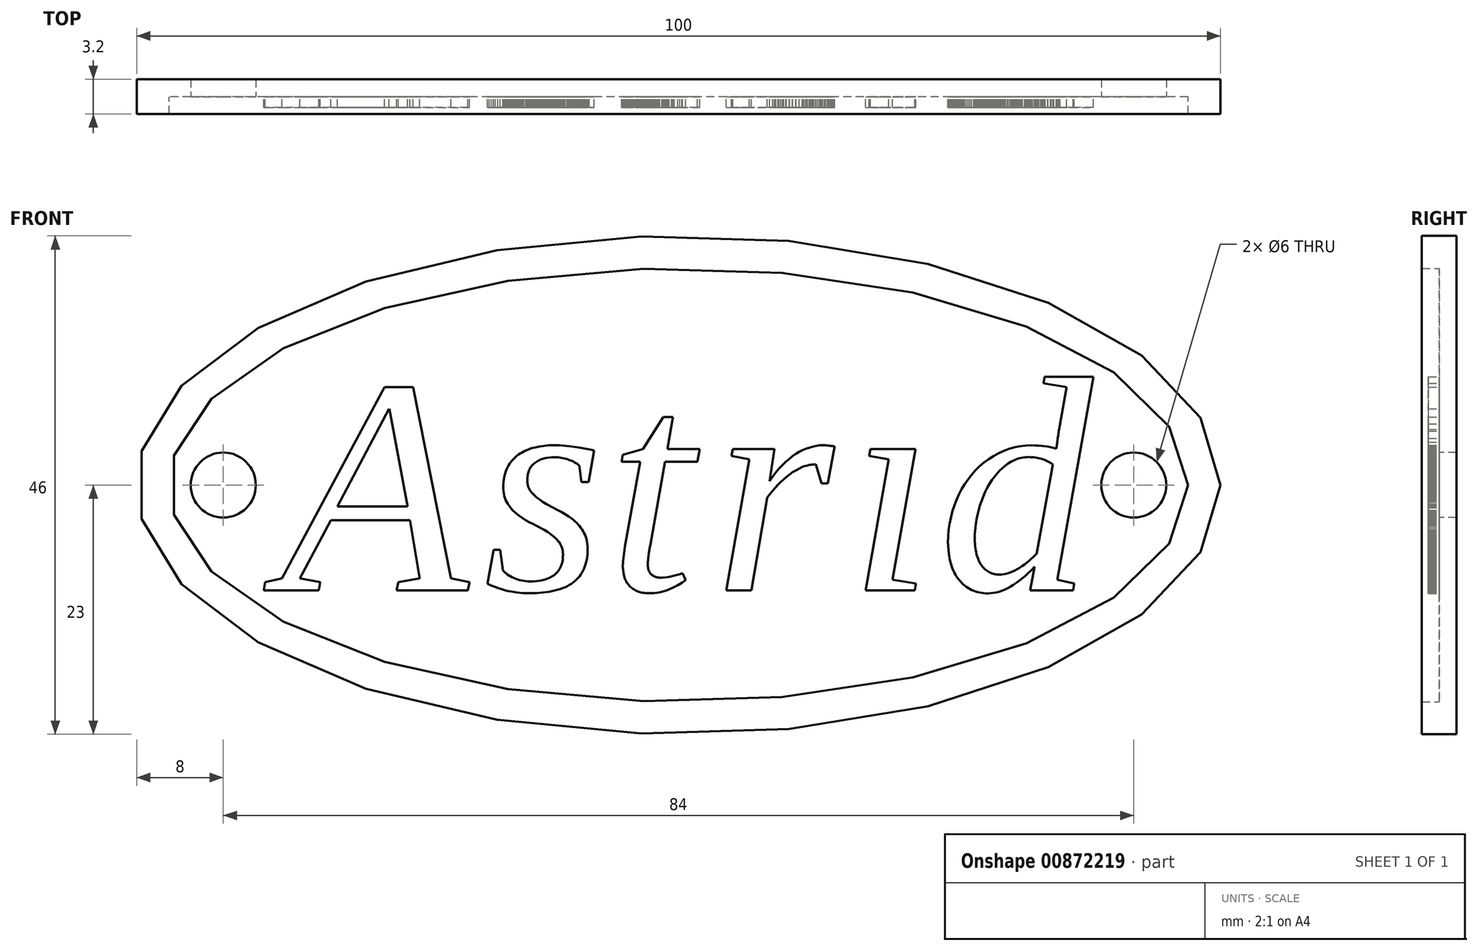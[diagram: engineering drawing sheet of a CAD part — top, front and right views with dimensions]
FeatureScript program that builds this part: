
annotation { "Feature Type Name" : "Feature", "Feature Type Description" : "" }
export const myFeature = defineFeature(function(context is Context, id is Id, definition is map)
    precondition{}
    {
        {
            var Q0;
            Q0=qCreatedBy(makeId("Front.planeOp"),FACE);
            var sketch = newSketch(context, id + "F0", { "sketchPlane" : qUnion([Q0])});
            skEllipse(sketch, "E0", {"center": v(0, 0) * mm, "majorRadius": 47 * mm, "minorRadius": 20 * mm, "majorAxis": v(1, 0)});
            skEllipse(sketch, "E1", {"center": v(0, 0) * mm, "majorRadius": 50 * mm, "minorRadius": 23 * mm, "majorAxis": v(1, 0)});
            skLineSegment(sketch, "E2", {"start": v(-81.12, 0) * mm, "end": v(85, 0) * mm, "construction": true});
            skPoint(sketch, "E2.startSnap0", {"position": v(-50, 0) * mm});
            skPoint(sketch, "E2.endSnap0", {"position": v(50, 0) * mm});
            skCircle(sketch, "E3", {"center": v(-42, 0) * mm, "radius": 3 * mm});
            skCircle(sketch, "E4", {"center": v(42, 0) * mm, "radius": 3 * mm});
            skLineSegment(sketch, "E5", {"start": v(-33.06, -8.97) * mm, "end": v(-33.2, -9.7) * mm});
            skLineSegment(sketch, "E6", {"start": v(-33.2, -9.7) * mm, "end": v(-38.27, -9.7) * mm});
            skLineSegment(sketch, "E7", {"start": v(-38.27, -9.7) * mm, "end": v(-38.14, -8.97) * mm});
            skLineSegment(sketch, "E8", {"start": v(-38.14, -8.97) * mm, "end": v(-36.58, -8.6) * mm});
            skLineSegment(sketch, "E9", {"start": v(-36.58, -8.6) * mm, "end": v(-27.12, 9.04) * mm});
            skLineSegment(sketch, "E10", {"start": v(-27.12, 9.04) * mm, "end": v(-24.47, 9.04) * mm});
            skLineSegment(sketch, "E11", {"start": v(-24.47, 9.04) * mm, "end": v(-21, -8.6) * mm});
            skLineSegment(sketch, "E12", {"start": v(-21, -8.6) * mm, "end": v(-19.27, -8.97) * mm});
            skLineSegment(sketch, "E13", {"start": v(-19.27, -8.97) * mm, "end": v(-19.43, -9.7) * mm});
            skLineSegment(sketch, "E14", {"start": v(-19.43, -9.7) * mm, "end": v(-26.01, -9.7) * mm});
            skLineSegment(sketch, "E15", {"start": v(-26.01, -9.7) * mm, "end": v(-25.86, -8.97) * mm});
            skLineSegment(sketch, "E16", {"start": v(-25.86, -8.97) * mm, "end": v(-23.88, -8.6) * mm});
            skLineSegment(sketch, "E17", {"start": v(-23.88, -8.6) * mm, "end": v(-24.77, -3.23) * mm});
            skLineSegment(sketch, "E18", {"start": v(-24.77, -3.23) * mm, "end": v(-32.09, -3.23) * mm});
            skLineSegment(sketch, "E19", {"start": v(-32.09, -3.23) * mm, "end": v(-34.93, -8.6) * mm});
            skLineSegment(sketch, "E20", {"start": v(-34.93, -8.6) * mm, "end": v(-33.06, -8.97) * mm});
            skLineSegment(sketch, "E21", {"start": v(-26.7, 7.05) * mm, "end": v(-31.46, -1.98) * mm});
            skLineSegment(sketch, "E22", {"start": v(-31.46, -1.98) * mm, "end": v(-24.99, -1.98) * mm});
            skLineSegment(sketch, "E23", {"start": v(-24.99, -1.98) * mm, "end": v(-26.7, 7.05) * mm});
            skLineSegment(sketch, "E24", {"start": v(-8.39, -5.88) * mm, "end": v(-8.4, -6.14) * mm});
            skLineSegment(sketch, "E25", {"start": v(-8.4, -6.14) * mm, "end": v(-8.4, -6.39) * mm});
            skLineSegment(sketch, "E26", {"start": v(-8.4, -6.39) * mm, "end": v(-8.43, -6.63) * mm});
            skLineSegment(sketch, "E27", {"start": v(-8.43, -6.63) * mm, "end": v(-8.47, -6.86) * mm});
            skLineSegment(sketch, "E28", {"start": v(-8.47, -6.86) * mm, "end": v(-8.52, -7.08) * mm});
            skLineSegment(sketch, "E29", {"start": v(-8.52, -7.08) * mm, "end": v(-8.57, -7.3) * mm});
            skLineSegment(sketch, "E30", {"start": v(-8.57, -7.3) * mm, "end": v(-8.64, -7.5) * mm});
            skLineSegment(sketch, "E31", {"start": v(-8.64, -7.5) * mm, "end": v(-8.72, -7.7) * mm});
            skLineSegment(sketch, "E32", {"start": v(-8.72, -7.7) * mm, "end": v(-8.8, -7.9) * mm});
            skLineSegment(sketch, "E33", {"start": v(-8.8, -7.9) * mm, "end": v(-8.9, -8.08) * mm});
            skLineSegment(sketch, "E34", {"start": v(-8.9, -8.08) * mm, "end": v(-9.01, -8.25) * mm});
            skLineSegment(sketch, "E35", {"start": v(-9.01, -8.25) * mm, "end": v(-9.13, -8.41) * mm});
            skLineSegment(sketch, "E36", {"start": v(-9.13, -8.41) * mm, "end": v(-9.26, -8.57) * mm});
            skLineSegment(sketch, "E37", {"start": v(-9.26, -8.57) * mm, "end": v(-9.4, -8.72) * mm});
            skLineSegment(sketch, "E38", {"start": v(-9.4, -8.72) * mm, "end": v(-9.56, -8.86) * mm});
            skLineSegment(sketch, "E39", {"start": v(-9.56, -8.86) * mm, "end": v(-9.72, -8.99) * mm});
            skLineSegment(sketch, "E40", {"start": v(-9.72, -8.99) * mm, "end": v(-9.89, -9.1) * mm});
            skLineSegment(sketch, "E41", {"start": v(-9.89, -9.1) * mm, "end": v(-10.07, -9.22) * mm});
            skLineSegment(sketch, "E42", {"start": v(-10.07, -9.22) * mm, "end": v(-10.26, -9.33) * mm});
            skLineSegment(sketch, "E43", {"start": v(-10.26, -9.33) * mm, "end": v(-10.47, -9.42) * mm});
            skLineSegment(sketch, "E44", {"start": v(-10.47, -9.42) * mm, "end": v(-10.68, -9.51) * mm});
            skLineSegment(sketch, "E45", {"start": v(-10.68, -9.51) * mm, "end": v(-10.9, -9.6) * mm});
            skLineSegment(sketch, "E46", {"start": v(-10.9, -9.6) * mm, "end": v(-11.14, -9.67) * mm});
            skLineSegment(sketch, "E47", {"start": v(-11.14, -9.67) * mm, "end": v(-11.4, -9.74) * mm});
            skLineSegment(sketch, "E48", {"start": v(-11.4, -9.74) * mm, "end": v(-11.65, -9.8) * mm});
            skLineSegment(sketch, "E49", {"start": v(-11.65, -9.8) * mm, "end": v(-11.92, -9.85) * mm});
            skLineSegment(sketch, "E50", {"start": v(-11.92, -9.85) * mm, "end": v(-12.2, -9.89) * mm});
            skLineSegment(sketch, "E51", {"start": v(-12.2, -9.89) * mm, "end": v(-12.49, -9.92) * mm});
            skLineSegment(sketch, "E52", {"start": v(-12.49, -9.92) * mm, "end": v(-13.1, -9.97) * mm});
            skLineSegment(sketch, "E53", {"start": v(-13.1, -9.97) * mm, "end": v(-13.75, -9.99) * mm});
            skLineSegment(sketch, "E54", {"start": v(-13.75, -9.99) * mm, "end": v(-14.36, -9.97) * mm});
            skLineSegment(sketch, "E55", {"start": v(-14.36, -9.97) * mm, "end": v(-14.94, -9.92) * mm});
            skLineSegment(sketch, "E56", {"start": v(-14.94, -9.92) * mm, "end": v(-15.48, -9.83) * mm});
            skLineSegment(sketch, "E57", {"start": v(-15.48, -9.83) * mm, "end": v(-15.74, -9.77) * mm});
            skLineSegment(sketch, "E58", {"start": v(-15.74, -9.77) * mm, "end": v(-15.99, -9.7) * mm});
            skLineSegment(sketch, "E59", {"start": v(-15.99, -9.7) * mm, "end": v(-16.46, -9.56) * mm});
            skLineSegment(sketch, "E60", {"start": v(-16.46, -9.56) * mm, "end": v(-16.68, -9.5) * mm});
            skLineSegment(sketch, "E61", {"start": v(-16.68, -9.5) * mm, "end": v(-16.9, -9.42) * mm});
            skLineSegment(sketch, "E62", {"start": v(-16.9, -9.42) * mm, "end": v(-17.1, -9.34) * mm});
            skLineSegment(sketch, "E63", {"start": v(-17.1, -9.34) * mm, "end": v(-17.28, -9.27) * mm});
            skLineSegment(sketch, "E64", {"start": v(-17.28, -9.27) * mm, "end": v(-17.46, -9.2) * mm});
            skLineSegment(sketch, "E65", {"start": v(-17.46, -9.2) * mm, "end": v(-17.64, -9.13) * mm});
            skLineSegment(sketch, "E66", {"start": v(-17.64, -9.13) * mm, "end": v(-17.07, -6) * mm});
            skLineSegment(sketch, "E67", {"start": v(-17.07, -6) * mm, "end": v(-16.44, -6) * mm});
            skLineSegment(sketch, "E68", {"start": v(-16.44, -6) * mm, "end": v(-16.2, -7.9) * mm});
            skLineSegment(sketch, "E69", {"start": v(-16.2, -7.9) * mm, "end": v(-16.11, -7.99) * mm});
            skLineSegment(sketch, "E70", {"start": v(-16.11, -7.99) * mm, "end": v(-16, -8.08) * mm});
            skLineSegment(sketch, "E71", {"start": v(-16, -8.08) * mm, "end": v(-15.9, -8.17) * mm});
            skLineSegment(sketch, "E72", {"start": v(-15.9, -8.17) * mm, "end": v(-15.77, -8.26) * mm});
            skLineSegment(sketch, "E73", {"start": v(-15.77, -8.26) * mm, "end": v(-15.64, -8.34) * mm});
            skLineSegment(sketch, "E74", {"start": v(-15.64, -8.34) * mm, "end": v(-15.5, -8.43) * mm});
            skLineSegment(sketch, "E75", {"start": v(-15.5, -8.43) * mm, "end": v(-15.35, -8.5) * mm});
            skLineSegment(sketch, "E76", {"start": v(-15.35, -8.5) * mm, "end": v(-15.2, -8.59) * mm});
            skLineSegment(sketch, "E77", {"start": v(-15.2, -8.59) * mm, "end": v(-15.03, -8.66) * mm});
            skLineSegment(sketch, "E78", {"start": v(-15.03, -8.66) * mm, "end": v(-14.85, -8.72) * mm});
            skLineSegment(sketch, "E79", {"start": v(-14.85, -8.72) * mm, "end": v(-14.67, -8.77) * mm});
            skLineSegment(sketch, "E80", {"start": v(-14.67, -8.77) * mm, "end": v(-14.49, -8.81) * mm});
            skLineSegment(sketch, "E81", {"start": v(-14.49, -8.81) * mm, "end": v(-14.3, -8.85) * mm});
            skLineSegment(sketch, "E82", {"start": v(-14.3, -8.85) * mm, "end": v(-14.1, -8.87) * mm});
            skLineSegment(sketch, "E83", {"start": v(-14.1, -8.87) * mm, "end": v(-13.9, -8.89) * mm});
            skLineSegment(sketch, "E84", {"start": v(-13.9, -8.89) * mm, "end": v(-13.7, -8.9) * mm});
            skLineSegment(sketch, "E85", {"start": v(-13.7, -8.9) * mm, "end": v(-13.39, -8.88) * mm});
            skLineSegment(sketch, "E86", {"start": v(-13.39, -8.88) * mm, "end": v(-13.1, -8.86) * mm});
            skLineSegment(sketch, "E87", {"start": v(-13.1, -8.86) * mm, "end": v(-12.8, -8.82) * mm});
            skLineSegment(sketch, "E88", {"start": v(-12.8, -8.82) * mm, "end": v(-12.52, -8.77) * mm});
            skLineSegment(sketch, "E89", {"start": v(-12.52, -8.77) * mm, "end": v(-12.38, -8.73) * mm});
            skLineSegment(sketch, "E90", {"start": v(-12.38, -8.73) * mm, "end": v(-12.25, -8.7) * mm});
            skLineSegment(sketch, "E91", {"start": v(-12.25, -8.7) * mm, "end": v(-12.12, -8.65) * mm});
            skLineSegment(sketch, "E92", {"start": v(-12.12, -8.65) * mm, "end": v(-12, -8.6) * mm});
            skLineSegment(sketch, "E93", {"start": v(-12, -8.6) * mm, "end": v(-11.88, -8.55) * mm});
            skLineSegment(sketch, "E94", {"start": v(-11.88, -8.55) * mm, "end": v(-11.76, -8.5) * mm});
            skLineSegment(sketch, "E95", {"start": v(-11.76, -8.5) * mm, "end": v(-11.65, -8.43) * mm});
            skLineSegment(sketch, "E96", {"start": v(-11.65, -8.43) * mm, "end": v(-11.55, -8.36) * mm});
            skLineSegment(sketch, "E97", {"start": v(-11.55, -8.36) * mm, "end": v(-11.45, -8.29) * mm});
            skLineSegment(sketch, "E98", {"start": v(-11.45, -8.29) * mm, "end": v(-11.35, -8.2) * mm});
            skLineSegment(sketch, "E99", {"start": v(-11.35, -8.2) * mm, "end": v(-11.26, -8.12) * mm});
            skLineSegment(sketch, "E100", {"start": v(-11.26, -8.12) * mm, "end": v(-11.18, -8.03) * mm});
            skLineSegment(sketch, "E101", {"start": v(-11.18, -8.03) * mm, "end": v(-11.1, -7.93) * mm});
            skLineSegment(sketch, "E102", {"start": v(-11.1, -7.93) * mm, "end": v(-11.02, -7.83) * mm});
            skLineSegment(sketch, "E103", {"start": v(-11.02, -7.83) * mm, "end": v(-10.96, -7.72) * mm});
            skLineSegment(sketch, "E104", {"start": v(-10.96, -7.72) * mm, "end": v(-10.9, -7.6) * mm});
            skLineSegment(sketch, "E105", {"start": v(-10.9, -7.6) * mm, "end": v(-10.84, -7.48) * mm});
            skLineSegment(sketch, "E106", {"start": v(-10.84, -7.48) * mm, "end": v(-10.8, -7.34) * mm});
            skLineSegment(sketch, "E107", {"start": v(-10.8, -7.34) * mm, "end": v(-10.75, -7.2) * mm});
            skLineSegment(sketch, "E108", {"start": v(-10.75, -7.2) * mm, "end": v(-10.72, -7.06) * mm});
            skLineSegment(sketch, "E109", {"start": v(-10.72, -7.06) * mm, "end": v(-10.7, -6.9) * mm});
            skLineSegment(sketch, "E110", {"start": v(-10.7, -6.9) * mm, "end": v(-10.67, -6.75) * mm});
            skLineSegment(sketch, "E111", {"start": v(-10.67, -6.75) * mm, "end": v(-10.66, -6.58) * mm});
            skLineSegment(sketch, "E112", {"start": v(-10.66, -6.58) * mm, "end": v(-10.66, -6.4) * mm});
            skLineSegment(sketch, "E113", {"start": v(-10.66, -6.4) * mm, "end": v(-10.67, -6.23) * mm});
            skLineSegment(sketch, "E114", {"start": v(-10.67, -6.23) * mm, "end": v(-10.67, -6.15) * mm});
            skLineSegment(sketch, "E115", {"start": v(-10.67, -6.15) * mm, "end": v(-10.69, -6.06) * mm});
            skLineSegment(sketch, "E116", {"start": v(-10.69, -6.06) * mm, "end": v(-10.7, -5.98) * mm});
            skLineSegment(sketch, "E117", {"start": v(-10.7, -5.98) * mm, "end": v(-10.72, -5.9) * mm});
            skLineSegment(sketch, "E118", {"start": v(-10.72, -5.9) * mm, "end": v(-10.74, -5.82) * mm});
            skLineSegment(sketch, "E119", {"start": v(-10.74, -5.82) * mm, "end": v(-10.76, -5.75) * mm});
            skLineSegment(sketch, "E120", {"start": v(-10.76, -5.75) * mm, "end": v(-10.8, -5.67) * mm});
            skLineSegment(sketch, "E121", {"start": v(-10.8, -5.67) * mm, "end": v(-10.82, -5.6) * mm});
            skLineSegment(sketch, "E122", {"start": v(-10.82, -5.6) * mm, "end": v(-10.86, -5.53) * mm});
            skLineSegment(sketch, "E123", {"start": v(-10.86, -5.53) * mm, "end": v(-10.9, -5.46) * mm});
            skLineSegment(sketch, "E124", {"start": v(-10.9, -5.46) * mm, "end": v(-10.93, -5.4) * mm});
            skLineSegment(sketch, "E125", {"start": v(-10.93, -5.4) * mm, "end": v(-10.98, -5.33) * mm});
            skLineSegment(sketch, "E126", {"start": v(-10.98, -5.33) * mm, "end": v(-11.03, -5.26) * mm});
            skLineSegment(sketch, "E127", {"start": v(-11.03, -5.26) * mm, "end": v(-11.08, -5.2) * mm});
            skLineSegment(sketch, "E128", {"start": v(-11.08, -5.2) * mm, "end": v(-11.18, -5.08) * mm});
            skLineSegment(sketch, "E129", {"start": v(-11.18, -5.08) * mm, "end": v(-11.3, -4.97) * mm});
            skLineSegment(sketch, "E130", {"start": v(-11.3, -4.97) * mm, "end": v(-11.4, -4.85) * mm});
            skLineSegment(sketch, "E131", {"start": v(-11.4, -4.85) * mm, "end": v(-11.53, -4.74) * mm});
            skLineSegment(sketch, "E132", {"start": v(-11.53, -4.74) * mm, "end": v(-11.66, -4.64) * mm});
            skLineSegment(sketch, "E133", {"start": v(-11.66, -4.64) * mm, "end": v(-11.94, -4.44) * mm});
            skLineSegment(sketch, "E134", {"start": v(-11.94, -4.44) * mm, "end": v(-12.09, -4.34) * mm});
            skLineSegment(sketch, "E135", {"start": v(-12.09, -4.34) * mm, "end": v(-12.4, -4.15) * mm});
            skLineSegment(sketch, "E136", {"start": v(-12.4, -4.15) * mm, "end": v(-13.07, -3.78) * mm});
            skLineSegment(sketch, "E137", {"start": v(-13.07, -3.78) * mm, "end": v(-13.42, -3.6) * mm});
            skLineSegment(sketch, "E138", {"start": v(-13.42, -3.6) * mm, "end": v(-13.77, -3.43) * mm});
            skLineSegment(sketch, "E139", {"start": v(-13.77, -3.43) * mm, "end": v(-14.1, -3.24) * mm});
            skLineSegment(sketch, "E140", {"start": v(-14.1, -3.24) * mm, "end": v(-14.43, -3.03) * mm});
            skLineSegment(sketch, "E141", {"start": v(-14.43, -3.03) * mm, "end": v(-14.74, -2.82) * mm});
            skLineSegment(sketch, "E142", {"start": v(-14.74, -2.82) * mm, "end": v(-15.03, -2.58) * mm});
            skLineSegment(sketch, "E143", {"start": v(-15.03, -2.58) * mm, "end": v(-15.3, -2.32) * mm});
            skLineSegment(sketch, "E144", {"start": v(-15.3, -2.32) * mm, "end": v(-15.54, -2.04) * mm});
            skLineSegment(sketch, "E145", {"start": v(-15.54, -2.04) * mm, "end": v(-15.76, -1.73) * mm});
            skLineSegment(sketch, "E146", {"start": v(-15.76, -1.73) * mm, "end": v(-15.86, -1.57) * mm});
            skLineSegment(sketch, "E147", {"start": v(-15.86, -1.57) * mm, "end": v(-15.94, -1.4) * mm});
            skLineSegment(sketch, "E148", {"start": v(-15.94, -1.4) * mm, "end": v(-16, -1.22) * mm});
            skLineSegment(sketch, "E149", {"start": v(-16, -1.22) * mm, "end": v(-16.07, -1.03) * mm});
            skLineSegment(sketch, "E150", {"start": v(-16.07, -1.03) * mm, "end": v(-16.1, -0.83) * mm});
            skLineSegment(sketch, "E151", {"start": v(-16.1, -0.83) * mm, "end": v(-16.14, -0.62) * mm});
            skLineSegment(sketch, "E152", {"start": v(-16.14, -0.62) * mm, "end": v(-16.16, -0.4) * mm});
            skLineSegment(sketch, "E153", {"start": v(-16.16, -0.4) * mm, "end": v(-16.17, -0.17) * mm});
            skLineSegment(sketch, "E154", {"start": v(-16.17, -0.17) * mm, "end": v(-16.16, 0.09) * mm});
            skLineSegment(sketch, "E155", {"start": v(-16.16, 0.09) * mm, "end": v(-16.14, 0.33) * mm});
            skLineSegment(sketch, "E156", {"start": v(-16.14, 0.33) * mm, "end": v(-16.11, 0.57) * mm});
            skLineSegment(sketch, "E157", {"start": v(-16.11, 0.57) * mm, "end": v(-16.07, 0.8) * mm});
            skLineSegment(sketch, "E158", {"start": v(-16.07, 0.8) * mm, "end": v(-16.02, 1.01) * mm});
            skLineSegment(sketch, "E159", {"start": v(-16.02, 1.01) * mm, "end": v(-15.96, 1.22) * mm});
            skLineSegment(sketch, "E160", {"start": v(-15.96, 1.22) * mm, "end": v(-15.88, 1.42) * mm});
            skLineSegment(sketch, "E161", {"start": v(-15.88, 1.42) * mm, "end": v(-15.8, 1.6) * mm});
            skLineSegment(sketch, "E162", {"start": v(-15.8, 1.6) * mm, "end": v(-15.7, 1.79) * mm});
            skLineSegment(sketch, "E163", {"start": v(-15.7, 1.79) * mm, "end": v(-15.58, 1.96) * mm});
            skLineSegment(sketch, "E164", {"start": v(-15.58, 1.96) * mm, "end": v(-15.47, 2.12) * mm});
            skLineSegment(sketch, "E165", {"start": v(-15.47, 2.12) * mm, "end": v(-15.34, 2.27) * mm});
            skLineSegment(sketch, "E166", {"start": v(-15.34, 2.27) * mm, "end": v(-15.2, 2.42) * mm});
            skLineSegment(sketch, "E167", {"start": v(-15.2, 2.42) * mm, "end": v(-15.07, 2.56) * mm});
            skLineSegment(sketch, "E168", {"start": v(-15.07, 2.56) * mm, "end": v(-14.92, 2.68) * mm});
            skLineSegment(sketch, "E169", {"start": v(-14.92, 2.68) * mm, "end": v(-14.77, 2.8) * mm});
            skLineSegment(sketch, "E170", {"start": v(-14.77, 2.8) * mm, "end": v(-14.6, 2.91) * mm});
            skLineSegment(sketch, "E171", {"start": v(-14.6, 2.91) * mm, "end": v(-14.43, 3.01) * mm});
            skLineSegment(sketch, "E172", {"start": v(-14.43, 3.01) * mm, "end": v(-14.25, 3.1) * mm});
            skLineSegment(sketch, "E173", {"start": v(-14.25, 3.1) * mm, "end": v(-14.07, 3.2) * mm});
            skLineSegment(sketch, "E174", {"start": v(-14.07, 3.2) * mm, "end": v(-13.88, 3.28) * mm});
            skLineSegment(sketch, "E175", {"start": v(-13.88, 3.28) * mm, "end": v(-13.69, 3.35) * mm});
            skLineSegment(sketch, "E176", {"start": v(-13.69, 3.35) * mm, "end": v(-13.49, 3.41) * mm});
            skLineSegment(sketch, "E177", {"start": v(-13.49, 3.41) * mm, "end": v(-13.28, 3.47) * mm});
            skLineSegment(sketch, "E178", {"start": v(-13.28, 3.47) * mm, "end": v(-12.85, 3.56) * mm});
            skLineSegment(sketch, "E179", {"start": v(-12.85, 3.56) * mm, "end": v(-12.41, 3.62) * mm});
            skLineSegment(sketch, "E180", {"start": v(-12.41, 3.62) * mm, "end": v(-11.97, 3.66) * mm});
            skLineSegment(sketch, "E181", {"start": v(-11.97, 3.66) * mm, "end": v(-11.5, 3.68) * mm});
            skLineSegment(sketch, "E182", {"start": v(-11.5, 3.68) * mm, "end": v(-11.01, 3.67) * mm});
            skLineSegment(sketch, "E183", {"start": v(-11.01, 3.67) * mm, "end": v(-10.05, 3.59) * mm});
            skLineSegment(sketch, "E184", {"start": v(-10.05, 3.59) * mm, "end": v(-9.58, 3.52) * mm});
            skLineSegment(sketch, "E185", {"start": v(-9.58, 3.52) * mm, "end": v(-9.12, 3.45) * mm});
            skLineSegment(sketch, "E186", {"start": v(-9.12, 3.45) * mm, "end": v(-8.22, 3.28) * mm});
            skLineSegment(sketch, "E187", {"start": v(-8.22, 3.28) * mm, "end": v(-7.79, 3.2) * mm});
            skLineSegment(sketch, "E188", {"start": v(-7.79, 3.2) * mm, "end": v(-8.3, 0.3) * mm});
            skLineSegment(sketch, "E189", {"start": v(-8.3, 0.3) * mm, "end": v(-8.95, 0.3) * mm});
            skLineSegment(sketch, "E190", {"start": v(-8.95, 0.3) * mm, "end": v(-9.15, 1.79) * mm});
            skLineSegment(sketch, "E191", {"start": v(-9.15, 1.79) * mm, "end": v(-9.25, 1.87) * mm});
            skLineSegment(sketch, "E192", {"start": v(-9.25, 1.87) * mm, "end": v(-9.36, 1.95) * mm});
            skLineSegment(sketch, "E193", {"start": v(-9.36, 1.95) * mm, "end": v(-9.47, 2.03) * mm});
            skLineSegment(sketch, "E194", {"start": v(-9.47, 2.03) * mm, "end": v(-9.6, 2.1) * mm});
            skLineSegment(sketch, "E195", {"start": v(-9.6, 2.1) * mm, "end": v(-9.72, 2.17) * mm});
            skLineSegment(sketch, "E196", {"start": v(-9.72, 2.17) * mm, "end": v(-9.86, 2.23) * mm});
            skLineSegment(sketch, "E197", {"start": v(-9.86, 2.23) * mm, "end": v(-10, 2.29) * mm});
            skLineSegment(sketch, "E198", {"start": v(-10, 2.29) * mm, "end": v(-10.15, 2.34) * mm});
            skLineSegment(sketch, "E199", {"start": v(-10.15, 2.34) * mm, "end": v(-10.3, 2.4) * mm});
            skLineSegment(sketch, "E200", {"start": v(-10.3, 2.4) * mm, "end": v(-10.45, 2.44) * mm});
            skLineSegment(sketch, "E201", {"start": v(-10.45, 2.44) * mm, "end": v(-10.6, 2.48) * mm});
            skLineSegment(sketch, "E202", {"start": v(-10.6, 2.48) * mm, "end": v(-10.77, 2.51) * mm});
            skLineSegment(sketch, "E203", {"start": v(-10.77, 2.51) * mm, "end": v(-10.94, 2.53) * mm});
            skLineSegment(sketch, "E204", {"start": v(-10.94, 2.53) * mm, "end": v(-11.1, 2.55) * mm});
            skLineSegment(sketch, "E205", {"start": v(-11.1, 2.55) * mm, "end": v(-11.28, 2.56) * mm});
            skLineSegment(sketch, "E206", {"start": v(-11.28, 2.56) * mm, "end": v(-11.45, 2.57) * mm});
            skLineSegment(sketch, "E207", {"start": v(-11.45, 2.57) * mm, "end": v(-11.73, 2.56) * mm});
            skLineSegment(sketch, "E208", {"start": v(-11.73, 2.56) * mm, "end": v(-12, 2.53) * mm});
            skLineSegment(sketch, "E209", {"start": v(-12, 2.53) * mm, "end": v(-12.24, 2.5) * mm});
            skLineSegment(sketch, "E210", {"start": v(-12.24, 2.5) * mm, "end": v(-12.36, 2.46) * mm});
            skLineSegment(sketch, "E211", {"start": v(-12.36, 2.46) * mm, "end": v(-12.47, 2.43) * mm});
            skLineSegment(sketch, "E212", {"start": v(-12.47, 2.43) * mm, "end": v(-12.59, 2.4) * mm});
            skLineSegment(sketch, "E213", {"start": v(-12.59, 2.4) * mm, "end": v(-12.7, 2.36) * mm});
            skLineSegment(sketch, "E214", {"start": v(-12.7, 2.36) * mm, "end": v(-12.8, 2.32) * mm});
            skLineSegment(sketch, "E215", {"start": v(-12.8, 2.32) * mm, "end": v(-12.9, 2.27) * mm});
            skLineSegment(sketch, "E216", {"start": v(-12.9, 2.27) * mm, "end": v(-13, 2.22) * mm});
            skLineSegment(sketch, "E217", {"start": v(-13, 2.22) * mm, "end": v(-13.1, 2.16) * mm});
            skLineSegment(sketch, "E218", {"start": v(-13.1, 2.16) * mm, "end": v(-13.18, 2.1) * mm});
            skLineSegment(sketch, "E219", {"start": v(-13.18, 2.1) * mm, "end": v(-13.27, 2.04) * mm});
            skLineSegment(sketch, "E220", {"start": v(-13.27, 2.04) * mm, "end": v(-13.35, 1.97) * mm});
            skLineSegment(sketch, "E221", {"start": v(-13.35, 1.97) * mm, "end": v(-13.43, 1.9) * mm});
            skLineSegment(sketch, "E222", {"start": v(-13.43, 1.9) * mm, "end": v(-13.5, 1.83) * mm});
            skLineSegment(sketch, "E223", {"start": v(-13.5, 1.83) * mm, "end": v(-13.56, 1.75) * mm});
            skLineSegment(sketch, "E224", {"start": v(-13.56, 1.75) * mm, "end": v(-13.63, 1.66) * mm});
            skLineSegment(sketch, "E225", {"start": v(-13.63, 1.66) * mm, "end": v(-13.68, 1.57) * mm});
            skLineSegment(sketch, "E226", {"start": v(-13.68, 1.57) * mm, "end": v(-13.73, 1.48) * mm});
            skLineSegment(sketch, "E227", {"start": v(-13.73, 1.48) * mm, "end": v(-13.78, 1.38) * mm});
            skLineSegment(sketch, "E228", {"start": v(-13.78, 1.38) * mm, "end": v(-13.82, 1.28) * mm});
            skLineSegment(sketch, "E229", {"start": v(-13.82, 1.28) * mm, "end": v(-13.85, 1.17) * mm});
            skLineSegment(sketch, "E230", {"start": v(-13.85, 1.17) * mm, "end": v(-13.88, 1.06) * mm});
            skLineSegment(sketch, "E231", {"start": v(-13.88, 1.06) * mm, "end": v(-13.9, 0.94) * mm});
            skLineSegment(sketch, "E232", {"start": v(-13.9, 0.94) * mm, "end": v(-13.92, 0.82) * mm});
            skLineSegment(sketch, "E233", {"start": v(-13.92, 0.82) * mm, "end": v(-13.94, 0.7) * mm});
            skLineSegment(sketch, "E234", {"start": v(-13.94, 0.7) * mm, "end": v(-13.94, 0.56) * mm});
            skLineSegment(sketch, "E235", {"start": v(-13.94, 0.56) * mm, "end": v(-13.95, 0.43) * mm});
            skLineSegment(sketch, "E236", {"start": v(-13.95, 0.43) * mm, "end": v(-13.94, 0.26) * mm});
            skLineSegment(sketch, "E237", {"start": v(-13.94, 0.26) * mm, "end": v(-13.93, 0.18) * mm});
            skLineSegment(sketch, "E238", {"start": v(-13.93, 0.18) * mm, "end": v(-13.92, 0.1) * mm});
            skLineSegment(sketch, "E239", {"start": v(-13.92, 0.1) * mm, "end": v(-13.9, 0.03) * mm});
            skLineSegment(sketch, "E240", {"start": v(-13.9, 0.03) * mm, "end": v(-13.9, -0.05) * mm});
            skLineSegment(sketch, "E241", {"start": v(-13.9, -0.05) * mm, "end": v(-13.87, -0.12) * mm});
            skLineSegment(sketch, "E242", {"start": v(-13.87, -0.12) * mm, "end": v(-13.85, -0.2) * mm});
            skLineSegment(sketch, "E243", {"start": v(-13.85, -0.2) * mm, "end": v(-13.82, -0.26) * mm});
            skLineSegment(sketch, "E244", {"start": v(-13.82, -0.26) * mm, "end": v(-13.79, -0.33) * mm});
            skLineSegment(sketch, "E245", {"start": v(-13.79, -0.33) * mm, "end": v(-13.76, -0.4) * mm});
            skLineSegment(sketch, "E246", {"start": v(-13.76, -0.4) * mm, "end": v(-13.72, -0.46) * mm});
            skLineSegment(sketch, "E247", {"start": v(-13.72, -0.46) * mm, "end": v(-13.68, -0.53) * mm});
            skLineSegment(sketch, "E248", {"start": v(-13.68, -0.53) * mm, "end": v(-13.64, -0.59) * mm});
            skLineSegment(sketch, "E249", {"start": v(-13.64, -0.59) * mm, "end": v(-13.6, -0.65) * mm});
            skLineSegment(sketch, "E250", {"start": v(-13.6, -0.65) * mm, "end": v(-13.54, -0.7) * mm});
            skLineSegment(sketch, "E251", {"start": v(-13.54, -0.7) * mm, "end": v(-13.32, -0.93) * mm});
            skLineSegment(sketch, "E252", {"start": v(-13.32, -0.93) * mm, "end": v(-13.08, -1.15) * mm});
            skLineSegment(sketch, "E253", {"start": v(-13.08, -1.15) * mm, "end": v(-12.8, -1.35) * mm});
            skLineSegment(sketch, "E254", {"start": v(-12.8, -1.35) * mm, "end": v(-12.5, -1.55) * mm});
            skLineSegment(sketch, "E255", {"start": v(-12.5, -1.55) * mm, "end": v(-12.19, -1.74) * mm});
            skLineSegment(sketch, "E256", {"start": v(-12.19, -1.74) * mm, "end": v(-11.52, -2.12) * mm});
            skLineSegment(sketch, "E257", {"start": v(-11.52, -2.12) * mm, "end": v(-11.17, -2.3) * mm});
            skLineSegment(sketch, "E258", {"start": v(-11.17, -2.3) * mm, "end": v(-10.82, -2.49) * mm});
            skLineSegment(sketch, "E259", {"start": v(-10.82, -2.49) * mm, "end": v(-10.48, -2.7) * mm});
            skLineSegment(sketch, "E260", {"start": v(-10.48, -2.7) * mm, "end": v(-10.15, -2.9) * mm});
            skLineSegment(sketch, "E261", {"start": v(-10.15, -2.9) * mm, "end": v(-9.83, -3.13) * mm});
            skLineSegment(sketch, "E262", {"start": v(-9.83, -3.13) * mm, "end": v(-9.68, -3.26) * mm});
            skLineSegment(sketch, "E263", {"start": v(-9.68, -3.26) * mm, "end": v(-9.53, -3.38) * mm});
            skLineSegment(sketch, "E264", {"start": v(-9.53, -3.38) * mm, "end": v(-9.4, -3.52) * mm});
            skLineSegment(sketch, "E265", {"start": v(-9.4, -3.52) * mm, "end": v(-9.26, -3.65) * mm});
            skLineSegment(sketch, "E266", {"start": v(-9.26, -3.65) * mm, "end": v(-9.13, -3.8) * mm});
            skLineSegment(sketch, "E267", {"start": v(-9.13, -3.8) * mm, "end": v(-9.02, -3.95) * mm});
            skLineSegment(sketch, "E268", {"start": v(-9.02, -3.95) * mm, "end": v(-8.9, -4.1) * mm});
            skLineSegment(sketch, "E269", {"start": v(-8.9, -4.1) * mm, "end": v(-8.8, -4.27) * mm});
            skLineSegment(sketch, "E270", {"start": v(-8.8, -4.27) * mm, "end": v(-8.7, -4.44) * mm});
            skLineSegment(sketch, "E271", {"start": v(-8.7, -4.44) * mm, "end": v(-8.62, -4.62) * mm});
            skLineSegment(sketch, "E272", {"start": v(-8.62, -4.62) * mm, "end": v(-8.55, -4.8) * mm});
            skLineSegment(sketch, "E273", {"start": v(-8.55, -4.8) * mm, "end": v(-8.49, -5) * mm});
            skLineSegment(sketch, "E274", {"start": v(-8.49, -5) * mm, "end": v(-8.44, -5.2) * mm});
            skLineSegment(sketch, "E275", {"start": v(-8.44, -5.2) * mm, "end": v(-8.41, -5.42) * mm});
            skLineSegment(sketch, "E276", {"start": v(-8.41, -5.42) * mm, "end": v(-8.4, -5.65) * mm});
            skLineSegment(sketch, "E277", {"start": v(-8.4, -5.65) * mm, "end": v(-8.39, -5.88) * mm});
            skLineSegment(sketch, "E278", {"start": v(-2.84, -7.3) * mm, "end": v(-2.84, -7.37) * mm});
            skLineSegment(sketch, "E279", {"start": v(-2.84, -7.37) * mm, "end": v(-2.83, -7.45) * mm});
            skLineSegment(sketch, "E280", {"start": v(-2.83, -7.45) * mm, "end": v(-2.83, -7.52) * mm});
            skLineSegment(sketch, "E281", {"start": v(-2.83, -7.52) * mm, "end": v(-2.82, -7.59) * mm});
            skLineSegment(sketch, "E282", {"start": v(-2.82, -7.59) * mm, "end": v(-2.8, -7.66) * mm});
            skLineSegment(sketch, "E283", {"start": v(-2.8, -7.66) * mm, "end": v(-2.8, -7.72) * mm});
            skLineSegment(sketch, "E284", {"start": v(-2.8, -7.72) * mm, "end": v(-2.78, -7.78) * mm});
            skLineSegment(sketch, "E285", {"start": v(-2.78, -7.78) * mm, "end": v(-2.76, -7.84) * mm});
            skLineSegment(sketch, "E286", {"start": v(-2.76, -7.84) * mm, "end": v(-2.74, -7.9) * mm});
            skLineSegment(sketch, "E287", {"start": v(-2.74, -7.9) * mm, "end": v(-2.72, -7.96) * mm});
            skLineSegment(sketch, "E288", {"start": v(-2.72, -7.96) * mm, "end": v(-2.7, -8) * mm});
            skLineSegment(sketch, "E289", {"start": v(-2.7, -8) * mm, "end": v(-2.67, -8.06) * mm});
            skLineSegment(sketch, "E290", {"start": v(-2.67, -8.06) * mm, "end": v(-2.64, -8.1) * mm});
            skLineSegment(sketch, "E291", {"start": v(-2.64, -8.1) * mm, "end": v(-2.6, -8.15) * mm});
            skLineSegment(sketch, "E292", {"start": v(-2.6, -8.15) * mm, "end": v(-2.57, -8.2) * mm});
            skLineSegment(sketch, "E293", {"start": v(-2.57, -8.2) * mm, "end": v(-2.53, -8.24) * mm});
            skLineSegment(sketch, "E294", {"start": v(-2.53, -8.24) * mm, "end": v(-2.5, -8.28) * mm});
            skLineSegment(sketch, "E295", {"start": v(-2.5, -8.28) * mm, "end": v(-2.45, -8.31) * mm});
            skLineSegment(sketch, "E296", {"start": v(-2.45, -8.31) * mm, "end": v(-2.4, -8.34) * mm});
            skLineSegment(sketch, "E297", {"start": v(-2.4, -8.34) * mm, "end": v(-2.36, -8.37) * mm});
            skLineSegment(sketch, "E298", {"start": v(-2.36, -8.37) * mm, "end": v(-2.32, -8.4) * mm});
            skLineSegment(sketch, "E299", {"start": v(-2.32, -8.4) * mm, "end": v(-2.27, -8.42) * mm});
            skLineSegment(sketch, "E300", {"start": v(-2.27, -8.42) * mm, "end": v(-2.22, -8.45) * mm});
            skLineSegment(sketch, "E301", {"start": v(-2.22, -8.45) * mm, "end": v(-2.17, -8.47) * mm});
            skLineSegment(sketch, "E302", {"start": v(-2.17, -8.47) * mm, "end": v(-2.12, -8.49) * mm});
            skLineSegment(sketch, "E303", {"start": v(-2.12, -8.49) * mm, "end": v(-2.07, -8.5) * mm});
            skLineSegment(sketch, "E304", {"start": v(-2.07, -8.5) * mm, "end": v(-2.01, -8.51) * mm});
            skLineSegment(sketch, "E305", {"start": v(-2.01, -8.51) * mm, "end": v(-1.96, -8.52) * mm});
            skLineSegment(sketch, "E306", {"start": v(-1.96, -8.52) * mm, "end": v(-1.9, -8.53) * mm});
            skLineSegment(sketch, "E307", {"start": v(-1.9, -8.53) * mm, "end": v(-1.85, -8.54) * mm});
            skLineSegment(sketch, "E308", {"start": v(-1.85, -8.54) * mm, "end": v(-1.79, -8.54) * mm});
            skLineSegment(sketch, "E309", {"start": v(-1.79, -8.54) * mm, "end": v(-1.73, -8.54) * mm});
            skLineSegment(sketch, "E310", {"start": v(-1.73, -8.54) * mm, "end": v(-1.43, -8.54) * mm});
            skLineSegment(sketch, "E311", {"start": v(-1.43, -8.54) * mm, "end": v(-1.15, -8.52) * mm});
            skLineSegment(sketch, "E312", {"start": v(-1.15, -8.52) * mm, "end": v(-0.89, -8.48) * mm});
            skLineSegment(sketch, "E313", {"start": v(-0.89, -8.48) * mm, "end": v(-0.63, -8.43) * mm});
            skLineSegment(sketch, "E314", {"start": v(-0.63, -8.43) * mm, "end": v(-0.38, -8.37) * mm});
            skLineSegment(sketch, "E315", {"start": v(-0.38, -8.37) * mm, "end": v(0.13, -8.22) * mm});
            skLineSegment(sketch, "E316", {"start": v(0.13, -8.22) * mm, "end": v(0.38, -8.13) * mm});
            skLineSegment(sketch, "E317", {"start": v(0.38, -8.13) * mm, "end": v(0.67, -8.78) * mm});
            skLineSegment(sketch, "E318", {"start": v(0.67, -8.78) * mm, "end": v(0.3, -9.02) * mm});
            skLineSegment(sketch, "E319", {"start": v(0.3, -9.02) * mm, "end": v(-0.07, -9.24) * mm});
            skLineSegment(sketch, "E320", {"start": v(-0.07, -9.24) * mm, "end": v(-0.47, -9.45) * mm});
            skLineSegment(sketch, "E321", {"start": v(-0.47, -9.45) * mm, "end": v(-0.88, -9.64) * mm});
            skLineSegment(sketch, "E322", {"start": v(-0.88, -9.64) * mm, "end": v(-1.1, -9.72) * mm});
            skLineSegment(sketch, "E323", {"start": v(-1.1, -9.72) * mm, "end": v(-1.31, -9.8) * mm});
            skLineSegment(sketch, "E324", {"start": v(-1.31, -9.8) * mm, "end": v(-1.54, -9.85) * mm});
            skLineSegment(sketch, "E325", {"start": v(-1.54, -9.85) * mm, "end": v(-1.77, -9.9) * mm});
            skLineSegment(sketch, "E326", {"start": v(-1.77, -9.9) * mm, "end": v(-2.01, -9.94) * mm});
            skLineSegment(sketch, "E327", {"start": v(-2.01, -9.94) * mm, "end": v(-2.26, -9.96) * mm});
            skLineSegment(sketch, "E328", {"start": v(-2.26, -9.96) * mm, "end": v(-2.52, -9.98) * mm});
            skLineSegment(sketch, "E329", {"start": v(-2.52, -9.98) * mm, "end": v(-2.78, -9.99) * mm});
            skLineSegment(sketch, "E330", {"start": v(-2.78, -9.99) * mm, "end": v(-2.92, -9.98) * mm});
            skLineSegment(sketch, "E331", {"start": v(-2.92, -9.98) * mm, "end": v(-3.06, -9.97) * mm});
            skLineSegment(sketch, "E332", {"start": v(-3.06, -9.97) * mm, "end": v(-3.2, -9.96) * mm});
            skLineSegment(sketch, "E333", {"start": v(-3.2, -9.96) * mm, "end": v(-3.33, -9.94) * mm});
            skLineSegment(sketch, "E334", {"start": v(-3.33, -9.94) * mm, "end": v(-3.46, -9.91) * mm});
            skLineSegment(sketch, "E335", {"start": v(-3.46, -9.91) * mm, "end": v(-3.58, -9.88) * mm});
            skLineSegment(sketch, "E336", {"start": v(-3.58, -9.88) * mm, "end": v(-3.7, -9.84) * mm});
            skLineSegment(sketch, "E337", {"start": v(-3.7, -9.84) * mm, "end": v(-3.8, -9.8) * mm});
            skLineSegment(sketch, "E338", {"start": v(-3.8, -9.8) * mm, "end": v(-3.92, -9.74) * mm});
            skLineSegment(sketch, "E339", {"start": v(-3.92, -9.74) * mm, "end": v(-4.02, -9.7) * mm});
            skLineSegment(sketch, "E340", {"start": v(-4.02, -9.7) * mm, "end": v(-4.12, -9.64) * mm});
            skLineSegment(sketch, "E341", {"start": v(-4.12, -9.64) * mm, "end": v(-4.22, -9.57) * mm});
            skLineSegment(sketch, "E342", {"start": v(-4.22, -9.57) * mm, "end": v(-4.3, -9.5) * mm});
            skLineSegment(sketch, "E343", {"start": v(-4.3, -9.5) * mm, "end": v(-4.4, -9.44) * mm});
            skLineSegment(sketch, "E344", {"start": v(-4.4, -9.44) * mm, "end": v(-4.48, -9.36) * mm});
            skLineSegment(sketch, "E345", {"start": v(-4.48, -9.36) * mm, "end": v(-4.56, -9.28) * mm});
            skLineSegment(sketch, "E346", {"start": v(-4.56, -9.28) * mm, "end": v(-4.63, -9.2) * mm});
            skLineSegment(sketch, "E347", {"start": v(-4.63, -9.2) * mm, "end": v(-4.7, -9.1) * mm});
            skLineSegment(sketch, "E348", {"start": v(-4.7, -9.1) * mm, "end": v(-4.76, -9.01) * mm});
            skLineSegment(sketch, "E349", {"start": v(-4.76, -9.01) * mm, "end": v(-4.81, -8.91) * mm});
            skLineSegment(sketch, "E350", {"start": v(-4.81, -8.91) * mm, "end": v(-4.87, -8.81) * mm});
            skLineSegment(sketch, "E351", {"start": v(-4.87, -8.81) * mm, "end": v(-4.92, -8.7) * mm});
            skLineSegment(sketch, "E352", {"start": v(-4.92, -8.7) * mm, "end": v(-4.96, -8.6) * mm});
            skLineSegment(sketch, "E353", {"start": v(-4.96, -8.6) * mm, "end": v(-5, -8.49) * mm});
            skLineSegment(sketch, "E354", {"start": v(-5, -8.49) * mm, "end": v(-5.06, -8.25) * mm});
            skLineSegment(sketch, "E355", {"start": v(-5.06, -8.25) * mm, "end": v(-5.1, -8) * mm});
            skLineSegment(sketch, "E356", {"start": v(-5.1, -8) * mm, "end": v(-5.13, -7.73) * mm});
            skLineSegment(sketch, "E357", {"start": v(-5.13, -7.73) * mm, "end": v(-5.14, -7.46) * mm});
            skLineSegment(sketch, "E358", {"start": v(-5.14, -7.46) * mm, "end": v(-5.13, -7.25) * mm});
            skLineSegment(sketch, "E359", {"start": v(-5.13, -7.25) * mm, "end": v(-5.12, -7.03) * mm});
            skLineSegment(sketch, "E360", {"start": v(-5.12, -7.03) * mm, "end": v(-5.1, -6.8) * mm});
            skLineSegment(sketch, "E361", {"start": v(-5.1, -6.8) * mm, "end": v(-5.07, -6.55) * mm});
            skLineSegment(sketch, "E362", {"start": v(-5.07, -6.55) * mm, "end": v(-5.03, -6.3) * mm});
            skLineSegment(sketch, "E363", {"start": v(-5.03, -6.3) * mm, "end": v(-4.96, -5.8) * mm});
            skLineSegment(sketch, "E364", {"start": v(-4.96, -5.8) * mm, "end": v(-4.92, -5.56) * mm});
            skLineSegment(sketch, "E365", {"start": v(-4.92, -5.56) * mm, "end": v(-3.54, 2.16) * mm});
            skLineSegment(sketch, "E366", {"start": v(-3.54, 2.16) * mm, "end": v(-5.25, 2.16) * mm});
            skLineSegment(sketch, "E367", {"start": v(-5.25, 2.16) * mm, "end": v(-5.14, 2.79) * mm});
            skLineSegment(sketch, "E368", {"start": v(-5.14, 2.79) * mm, "end": v(-3.3, 3.33) * mm});
            skLineSegment(sketch, "E369", {"start": v(-3.3, 3.33) * mm, "end": v(-1.4, 6.28) * mm});
            skLineSegment(sketch, "E370", {"start": v(-1.4, 6.28) * mm, "end": v(-0.5, 6.28) * mm});
            skLineSegment(sketch, "E371", {"start": v(-0.5, 6.28) * mm, "end": v(-1.02, 3.33) * mm});
            skLineSegment(sketch, "E372", {"start": v(-1.02, 3.33) * mm, "end": v(1.96, 3.33) * mm});
            skLineSegment(sketch, "E373", {"start": v(1.96, 3.33) * mm, "end": v(1.74, 2.16) * mm});
            skLineSegment(sketch, "E374", {"start": v(1.74, 2.16) * mm, "end": v(-1.24, 2.16) * mm});
            skLineSegment(sketch, "E375", {"start": v(-1.24, 2.16) * mm, "end": v(-2.59, -5.45) * mm});
            skLineSegment(sketch, "E376", {"start": v(-2.59, -5.45) * mm, "end": v(-2.64, -5.73) * mm});
            skLineSegment(sketch, "E377", {"start": v(-2.64, -5.73) * mm, "end": v(-2.73, -6.26) * mm});
            skLineSegment(sketch, "E378", {"start": v(-2.73, -6.26) * mm, "end": v(-2.77, -6.5) * mm});
            skLineSegment(sketch, "E379", {"start": v(-2.77, -6.5) * mm, "end": v(-2.78, -6.62) * mm});
            skLineSegment(sketch, "E380", {"start": v(-2.78, -6.62) * mm, "end": v(-2.8, -6.74) * mm});
            skLineSegment(sketch, "E381", {"start": v(-2.8, -6.74) * mm, "end": v(-2.8, -6.84) * mm});
            skLineSegment(sketch, "E382", {"start": v(-2.8, -6.84) * mm, "end": v(-2.82, -6.95) * mm});
            skLineSegment(sketch, "E383", {"start": v(-2.82, -6.95) * mm, "end": v(-2.83, -7.04) * mm});
            skLineSegment(sketch, "E384", {"start": v(-2.83, -7.04) * mm, "end": v(-2.83, -7.13) * mm});
            skLineSegment(sketch, "E385", {"start": v(-2.83, -7.13) * mm, "end": v(-2.84, -7.22) * mm});
            skLineSegment(sketch, "E386", {"start": v(-2.84, -7.22) * mm, "end": v(-2.84, -7.3) * mm});
            skLineSegment(sketch, "E387", {"start": v(13.3, 3.68) * mm, "end": v(13.44, 3.67) * mm});
            skLineSegment(sketch, "E388", {"start": v(13.44, 3.67) * mm, "end": v(13.59, 3.67) * mm});
            skLineSegment(sketch, "E389", {"start": v(13.59, 3.67) * mm, "end": v(13.74, 3.65) * mm});
            skLineSegment(sketch, "E390", {"start": v(13.74, 3.65) * mm, "end": v(13.9, 3.63) * mm});
            skLineSegment(sketch, "E391", {"start": v(13.9, 3.63) * mm, "end": v(13.99, 3.63) * mm});
            skLineSegment(sketch, "E392", {"start": v(13.99, 3.63) * mm, "end": v(14.06, 3.62) * mm});
            skLineSegment(sketch, "E393", {"start": v(14.06, 3.62) * mm, "end": v(14.13, 3.61) * mm});
            skLineSegment(sketch, "E394", {"start": v(14.13, 3.61) * mm, "end": v(14.16, 3.6) * mm});
            skLineSegment(sketch, "E395", {"start": v(14.16, 3.6) * mm, "end": v(14.2, 3.6) * mm});
            skLineSegment(sketch, "E396", {"start": v(14.2, 3.6) * mm, "end": v(14.22, 3.6) * mm});
            skLineSegment(sketch, "E397", {"start": v(14.22, 3.6) * mm, "end": v(14.25, 3.6) * mm});
            skLineSegment(sketch, "E398", {"start": v(14.25, 3.6) * mm, "end": v(14.28, 3.59) * mm});
            skLineSegment(sketch, "E399", {"start": v(14.28, 3.59) * mm, "end": v(14.3, 3.58) * mm});
            skLineSegment(sketch, "E400", {"start": v(14.3, 3.58) * mm, "end": v(14.33, 3.58) * mm});
            skLineSegment(sketch, "E401", {"start": v(14.33, 3.58) * mm, "end": v(14.35, 3.57) * mm});
            skLineSegment(sketch, "E402", {"start": v(14.35, 3.57) * mm, "end": v(14.37, 3.57) * mm});
            skLineSegment(sketch, "E403", {"start": v(14.37, 3.57) * mm, "end": v(14.4, 3.56) * mm});
            skLineSegment(sketch, "E404", {"start": v(14.4, 3.56) * mm, "end": v(13.78, 0.15) * mm});
            skLineSegment(sketch, "E405", {"start": v(13.78, 0.15) * mm, "end": v(13.18, 0.15) * mm});
            skLineSegment(sketch, "E406", {"start": v(13.18, 0.15) * mm, "end": v(12.66, 1.91) * mm});
            skLineSegment(sketch, "E407", {"start": v(12.66, 1.91) * mm, "end": v(12.5, 1.91) * mm});
            skLineSegment(sketch, "E408", {"start": v(12.5, 1.91) * mm, "end": v(12.35, 1.9) * mm});
            skLineSegment(sketch, "E409", {"start": v(12.35, 1.9) * mm, "end": v(12.2, 1.88) * mm});
            skLineSegment(sketch, "E410", {"start": v(12.2, 1.88) * mm, "end": v(12.05, 1.85) * mm});
            skLineSegment(sketch, "E411", {"start": v(12.05, 1.85) * mm, "end": v(11.9, 1.82) * mm});
            skLineSegment(sketch, "E412", {"start": v(11.9, 1.82) * mm, "end": v(11.74, 1.77) * mm});
            skLineSegment(sketch, "E413", {"start": v(11.74, 1.77) * mm, "end": v(11.59, 1.72) * mm});
            skLineSegment(sketch, "E414", {"start": v(11.59, 1.72) * mm, "end": v(11.44, 1.66) * mm});
            skLineSegment(sketch, "E415", {"start": v(11.44, 1.66) * mm, "end": v(11.13, 1.53) * mm});
            skLineSegment(sketch, "E416", {"start": v(11.13, 1.53) * mm, "end": v(10.84, 1.37) * mm});
            skLineSegment(sketch, "E417", {"start": v(10.84, 1.37) * mm, "end": v(10.54, 1.19) * mm});
            skLineSegment(sketch, "E418", {"start": v(10.54, 1.19) * mm, "end": v(10.26, 0.98) * mm});
            skLineSegment(sketch, "E419", {"start": v(10.26, 0.98) * mm, "end": v(9.98, 0.77) * mm});
            skLineSegment(sketch, "E420", {"start": v(9.98, 0.77) * mm, "end": v(9.7, 0.53) * mm});
            skLineSegment(sketch, "E421", {"start": v(9.7, 0.53) * mm, "end": v(9.43, 0.28) * mm});
            skLineSegment(sketch, "E422", {"start": v(9.43, 0.28) * mm, "end": v(9.16, 0.01) * mm});
            skLineSegment(sketch, "E423", {"start": v(9.16, 0.01) * mm, "end": v(8.9, -0.27) * mm});
            skLineSegment(sketch, "E424", {"start": v(8.9, -0.27) * mm, "end": v(8.42, -0.86) * mm});
            skLineSegment(sketch, "E425", {"start": v(8.42, -0.86) * mm, "end": v(8.2, -1.17) * mm});
            skLineSegment(sketch, "E426", {"start": v(8.2, -1.17) * mm, "end": v(6.7, -9.7) * mm});
            skLineSegment(sketch, "E427", {"start": v(6.7, -9.7) * mm, "end": v(4.4, -9.7) * mm});
            skLineSegment(sketch, "E428", {"start": v(4.4, -9.7) * mm, "end": v(6.53, 2.36) * mm});
            skLineSegment(sketch, "E429", {"start": v(6.53, 2.36) * mm, "end": v(4.89, 2.7) * mm});
            skLineSegment(sketch, "E430", {"start": v(4.89, 2.7) * mm, "end": v(5, 3.33) * mm});
            skLineSegment(sketch, "E431", {"start": v(5, 3.33) * mm, "end": v(8.84, 3.33) * mm});
            skLineSegment(sketch, "E432", {"start": v(8.84, 3.33) * mm, "end": v(8.41, 0.39) * mm});
            skLineSegment(sketch, "E433", {"start": v(8.41, 0.39) * mm, "end": v(8.7, 0.8) * mm});
            skLineSegment(sketch, "E434", {"start": v(8.7, 0.8) * mm, "end": v(8.98, 1.17) * mm});
            skLineSegment(sketch, "E435", {"start": v(8.98, 1.17) * mm, "end": v(9.28, 1.52) * mm});
            skLineSegment(sketch, "E436", {"start": v(9.28, 1.52) * mm, "end": v(9.58, 1.84) * mm});
            skLineSegment(sketch, "E437", {"start": v(9.58, 1.84) * mm, "end": v(9.89, 2.14) * mm});
            skLineSegment(sketch, "E438", {"start": v(9.89, 2.14) * mm, "end": v(10.2, 2.41) * mm});
            skLineSegment(sketch, "E439", {"start": v(10.2, 2.41) * mm, "end": v(10.51, 2.66) * mm});
            skLineSegment(sketch, "E440", {"start": v(10.51, 2.66) * mm, "end": v(10.83, 2.87) * mm});
            skLineSegment(sketch, "E441", {"start": v(10.83, 2.87) * mm, "end": v(11.14, 3.06) * mm});
            skLineSegment(sketch, "E442", {"start": v(11.14, 3.06) * mm, "end": v(11.45, 3.22) * mm});
            skLineSegment(sketch, "E443", {"start": v(11.45, 3.22) * mm, "end": v(11.76, 3.36) * mm});
            skLineSegment(sketch, "E444", {"start": v(11.76, 3.36) * mm, "end": v(12.07, 3.47) * mm});
            skLineSegment(sketch, "E445", {"start": v(12.07, 3.47) * mm, "end": v(12.39, 3.56) * mm});
            skLineSegment(sketch, "E446", {"start": v(12.39, 3.56) * mm, "end": v(12.7, 3.62) * mm});
            skLineSegment(sketch, "E447", {"start": v(12.7, 3.62) * mm, "end": v(12.85, 3.65) * mm});
            skLineSegment(sketch, "E448", {"start": v(12.85, 3.65) * mm, "end": v(13, 3.66) * mm});
            skLineSegment(sketch, "E449", {"start": v(13, 3.66) * mm, "end": v(13.15, 3.67) * mm});
            skLineSegment(sketch, "E450", {"start": v(13.15, 3.67) * mm, "end": v(13.3, 3.68) * mm});
            skLineSegment(sketch, "E451", {"start": v(19.73, -8.74) * mm, "end": v(21.9, -9.08) * mm});
            skLineSegment(sketch, "E452", {"start": v(21.9, -9.08) * mm, "end": v(21.8, -9.7) * mm});
            skLineSegment(sketch, "E453", {"start": v(21.8, -9.7) * mm, "end": v(17.26, -9.7) * mm});
            skLineSegment(sketch, "E454", {"start": v(17.26, -9.7) * mm, "end": v(19.38, 2.36) * mm});
            skLineSegment(sketch, "E455", {"start": v(19.38, 2.36) * mm, "end": v(17.6, 2.7) * mm});
            skLineSegment(sketch, "E456", {"start": v(17.6, 2.7) * mm, "end": v(17.7, 3.33) * mm});
            skLineSegment(sketch, "E457", {"start": v(17.7, 3.33) * mm, "end": v(21.85, 3.33) * mm});
            skLineSegment(sketch, "E458", {"start": v(21.85, 3.33) * mm, "end": v(19.73, -8.74) * mm});
            skLineSegment(sketch, "E459", {"start": v(22.71, 7.59) * mm, "end": v(22.71, 7.51) * mm});
            skLineSegment(sketch, "E460", {"start": v(22.71, 7.51) * mm, "end": v(22.7, 7.44) * mm});
            skLineSegment(sketch, "E461", {"start": v(22.7, 7.44) * mm, "end": v(22.7, 7.36) * mm});
            skLineSegment(sketch, "E462", {"start": v(22.7, 7.36) * mm, "end": v(22.68, 7.29) * mm});
            skLineSegment(sketch, "E463", {"start": v(22.68, 7.29) * mm, "end": v(22.66, 7.22) * mm});
            skLineSegment(sketch, "E464", {"start": v(22.66, 7.22) * mm, "end": v(22.64, 7.14) * mm});
            skLineSegment(sketch, "E465", {"start": v(22.64, 7.14) * mm, "end": v(22.62, 7.07) * mm});
            skLineSegment(sketch, "E466", {"start": v(22.62, 7.07) * mm, "end": v(22.59, 7) * mm});
            skLineSegment(sketch, "E467", {"start": v(22.59, 7) * mm, "end": v(22.56, 6.94) * mm});
            skLineSegment(sketch, "E468", {"start": v(22.56, 6.94) * mm, "end": v(22.53, 6.88) * mm});
            skLineSegment(sketch, "E469", {"start": v(22.53, 6.88) * mm, "end": v(22.5, 6.81) * mm});
            skLineSegment(sketch, "E470", {"start": v(22.5, 6.81) * mm, "end": v(22.45, 6.75) * mm});
            skLineSegment(sketch, "E471", {"start": v(22.45, 6.75) * mm, "end": v(22.41, 6.7) * mm});
            skLineSegment(sketch, "E472", {"start": v(22.41, 6.7) * mm, "end": v(22.37, 6.64) * mm});
            skLineSegment(sketch, "E473", {"start": v(22.37, 6.64) * mm, "end": v(22.32, 6.59) * mm});
            skLineSegment(sketch, "E474", {"start": v(22.32, 6.59) * mm, "end": v(22.27, 6.53) * mm});
            skLineSegment(sketch, "E475", {"start": v(22.27, 6.53) * mm, "end": v(22.22, 6.48) * mm});
            skLineSegment(sketch, "E476", {"start": v(22.22, 6.48) * mm, "end": v(22.16, 6.43) * mm});
            skLineSegment(sketch, "E477", {"start": v(22.16, 6.43) * mm, "end": v(22.1, 6.39) * mm});
            skLineSegment(sketch, "E478", {"start": v(22.1, 6.39) * mm, "end": v(22.04, 6.35) * mm});
            skLineSegment(sketch, "E479", {"start": v(22.04, 6.35) * mm, "end": v(21.98, 6.3) * mm});
            skLineSegment(sketch, "E480", {"start": v(21.98, 6.3) * mm, "end": v(21.92, 6.27) * mm});
            skLineSegment(sketch, "E481", {"start": v(21.92, 6.27) * mm, "end": v(21.85, 6.23) * mm});
            skLineSegment(sketch, "E482", {"start": v(21.85, 6.23) * mm, "end": v(21.78, 6.2) * mm});
            skLineSegment(sketch, "E483", {"start": v(21.78, 6.2) * mm, "end": v(21.71, 6.17) * mm});
            skLineSegment(sketch, "E484", {"start": v(21.71, 6.17) * mm, "end": v(21.64, 6.15) * mm});
            skLineSegment(sketch, "E485", {"start": v(21.64, 6.15) * mm, "end": v(21.57, 6.13) * mm});
            skLineSegment(sketch, "E486", {"start": v(21.57, 6.13) * mm, "end": v(21.5, 6.12) * mm});
            skLineSegment(sketch, "E487", {"start": v(21.5, 6.12) * mm, "end": v(21.43, 6.1) * mm});
            skLineSegment(sketch, "E488", {"start": v(21.43, 6.1) * mm, "end": v(21.35, 6.1) * mm});
            skLineSegment(sketch, "E489", {"start": v(21.35, 6.1) * mm, "end": v(21.28, 6.1) * mm});
            skLineSegment(sketch, "E490", {"start": v(21.28, 6.1) * mm, "end": v(21.2, 6.09) * mm});
            skLineSegment(sketch, "E491", {"start": v(21.2, 6.09) * mm, "end": v(21.12, 6.1) * mm});
            skLineSegment(sketch, "E492", {"start": v(21.12, 6.1) * mm, "end": v(21.05, 6.1) * mm});
            skLineSegment(sketch, "E493", {"start": v(21.05, 6.1) * mm, "end": v(20.98, 6.1) * mm});
            skLineSegment(sketch, "E494", {"start": v(20.98, 6.1) * mm, "end": v(20.9, 6.12) * mm});
            skLineSegment(sketch, "E495", {"start": v(20.9, 6.12) * mm, "end": v(20.83, 6.13) * mm});
            skLineSegment(sketch, "E496", {"start": v(20.83, 6.13) * mm, "end": v(20.76, 6.15) * mm});
            skLineSegment(sketch, "E497", {"start": v(20.76, 6.15) * mm, "end": v(20.69, 6.17) * mm});
            skLineSegment(sketch, "E498", {"start": v(20.69, 6.17) * mm, "end": v(20.62, 6.2) * mm});
            skLineSegment(sketch, "E499", {"start": v(20.62, 6.2) * mm, "end": v(20.49, 6.27) * mm});
            skLineSegment(sketch, "E500", {"start": v(20.49, 6.27) * mm, "end": v(20.37, 6.35) * mm});
            skLineSegment(sketch, "E501", {"start": v(20.37, 6.35) * mm, "end": v(20.25, 6.43) * mm});
            skLineSegment(sketch, "E502", {"start": v(20.25, 6.43) * mm, "end": v(20.15, 6.53) * mm});
            skLineSegment(sketch, "E503", {"start": v(20.15, 6.53) * mm, "end": v(20.05, 6.64) * mm});
            skLineSegment(sketch, "E504", {"start": v(20.05, 6.64) * mm, "end": v(19.96, 6.75) * mm});
            skLineSegment(sketch, "E505", {"start": v(19.96, 6.75) * mm, "end": v(19.88, 6.88) * mm});
            skLineSegment(sketch, "E506", {"start": v(19.88, 6.88) * mm, "end": v(19.81, 7) * mm});
            skLineSegment(sketch, "E507", {"start": v(19.81, 7) * mm, "end": v(19.79, 7.07) * mm});
            skLineSegment(sketch, "E508", {"start": v(19.79, 7.07) * mm, "end": v(19.77, 7.14) * mm});
            skLineSegment(sketch, "E509", {"start": v(19.77, 7.14) * mm, "end": v(19.75, 7.22) * mm});
            skLineSegment(sketch, "E510", {"start": v(19.75, 7.22) * mm, "end": v(19.73, 7.29) * mm});
            skLineSegment(sketch, "E511", {"start": v(19.73, 7.29) * mm, "end": v(19.72, 7.36) * mm});
            skLineSegment(sketch, "E512", {"start": v(19.72, 7.36) * mm, "end": v(19.7, 7.44) * mm});
            skLineSegment(sketch, "E513", {"start": v(19.7, 7.44) * mm, "end": v(19.7, 7.51) * mm});
            skLineSegment(sketch, "E514", {"start": v(19.7, 7.51) * mm, "end": v(19.7, 7.59) * mm});
            skLineSegment(sketch, "E515", {"start": v(19.7, 7.59) * mm, "end": v(19.7, 7.66) * mm});
            skLineSegment(sketch, "E516", {"start": v(19.7, 7.66) * mm, "end": v(19.7, 7.74) * mm});
            skLineSegment(sketch, "E517", {"start": v(19.7, 7.74) * mm, "end": v(19.72, 7.81) * mm});
            skLineSegment(sketch, "E518", {"start": v(19.72, 7.81) * mm, "end": v(19.73, 7.88) * mm});
            skLineSegment(sketch, "E519", {"start": v(19.73, 7.88) * mm, "end": v(19.75, 7.96) * mm});
            skLineSegment(sketch, "E520", {"start": v(19.75, 7.96) * mm, "end": v(19.77, 8.03) * mm});
            skLineSegment(sketch, "E521", {"start": v(19.77, 8.03) * mm, "end": v(19.79, 8.1) * mm});
            skLineSegment(sketch, "E522", {"start": v(19.79, 8.1) * mm, "end": v(19.81, 8.17) * mm});
            skLineSegment(sketch, "E523", {"start": v(19.81, 8.17) * mm, "end": v(19.85, 8.24) * mm});
            skLineSegment(sketch, "E524", {"start": v(19.85, 8.24) * mm, "end": v(19.88, 8.3) * mm});
            skLineSegment(sketch, "E525", {"start": v(19.88, 8.3) * mm, "end": v(19.92, 8.37) * mm});
            skLineSegment(sketch, "E526", {"start": v(19.92, 8.37) * mm, "end": v(19.96, 8.43) * mm});
            skLineSegment(sketch, "E527", {"start": v(19.96, 8.43) * mm, "end": v(20, 8.49) * mm});
            skLineSegment(sketch, "E528", {"start": v(20, 8.49) * mm, "end": v(20.05, 8.55) * mm});
            skLineSegment(sketch, "E529", {"start": v(20.05, 8.55) * mm, "end": v(20.1, 8.6) * mm});
            skLineSegment(sketch, "E530", {"start": v(20.1, 8.6) * mm, "end": v(20.15, 8.65) * mm});
            skLineSegment(sketch, "E531", {"start": v(20.15, 8.65) * mm, "end": v(20.2, 8.7) * mm});
            skLineSegment(sketch, "E532", {"start": v(20.2, 8.7) * mm, "end": v(20.25, 8.75) * mm});
            skLineSegment(sketch, "E533", {"start": v(20.25, 8.75) * mm, "end": v(20.31, 8.8) * mm});
            skLineSegment(sketch, "E534", {"start": v(20.31, 8.8) * mm, "end": v(20.37, 8.84) * mm});
            skLineSegment(sketch, "E535", {"start": v(20.37, 8.84) * mm, "end": v(20.43, 8.88) * mm});
            skLineSegment(sketch, "E536", {"start": v(20.43, 8.88) * mm, "end": v(20.49, 8.91) * mm});
            skLineSegment(sketch, "E537", {"start": v(20.49, 8.91) * mm, "end": v(20.55, 8.94) * mm});
            skLineSegment(sketch, "E538", {"start": v(20.55, 8.94) * mm, "end": v(20.62, 8.97) * mm});
            skLineSegment(sketch, "E539", {"start": v(20.62, 8.97) * mm, "end": v(20.69, 9) * mm});
            skLineSegment(sketch, "E540", {"start": v(20.69, 9) * mm, "end": v(20.76, 9.03) * mm});
            skLineSegment(sketch, "E541", {"start": v(20.76, 9.03) * mm, "end": v(20.83, 9.05) * mm});
            skLineSegment(sketch, "E542", {"start": v(20.83, 9.05) * mm, "end": v(20.9, 9.07) * mm});
            skLineSegment(sketch, "E543", {"start": v(20.9, 9.07) * mm, "end": v(20.98, 9.08) * mm});
            skLineSegment(sketch, "E544", {"start": v(20.98, 9.08) * mm, "end": v(21.05, 9.1) * mm});
            skLineSegment(sketch, "E545", {"start": v(21.05, 9.1) * mm, "end": v(21.12, 9.1) * mm});
            skLineSegment(sketch, "E546", {"start": v(21.12, 9.1) * mm, "end": v(21.2, 9.1) * mm});
            skLineSegment(sketch, "E547", {"start": v(21.2, 9.1) * mm, "end": v(21.28, 9.1) * mm});
            skLineSegment(sketch, "E548", {"start": v(21.28, 9.1) * mm, "end": v(21.35, 9.1) * mm});
            skLineSegment(sketch, "E549", {"start": v(21.35, 9.1) * mm, "end": v(21.43, 9.08) * mm});
            skLineSegment(sketch, "E550", {"start": v(21.43, 9.08) * mm, "end": v(21.5, 9.07) * mm});
            skLineSegment(sketch, "E551", {"start": v(21.5, 9.07) * mm, "end": v(21.57, 9.05) * mm});
            skLineSegment(sketch, "E552", {"start": v(21.57, 9.05) * mm, "end": v(21.64, 9.03) * mm});
            skLineSegment(sketch, "E553", {"start": v(21.64, 9.03) * mm, "end": v(21.71, 9) * mm});
            skLineSegment(sketch, "E554", {"start": v(21.71, 9) * mm, "end": v(21.78, 8.97) * mm});
            skLineSegment(sketch, "E555", {"start": v(21.78, 8.97) * mm, "end": v(21.85, 8.94) * mm});
            skLineSegment(sketch, "E556", {"start": v(21.85, 8.94) * mm, "end": v(21.92, 8.91) * mm});
            skLineSegment(sketch, "E557", {"start": v(21.92, 8.91) * mm, "end": v(21.98, 8.88) * mm});
            skLineSegment(sketch, "E558", {"start": v(21.98, 8.88) * mm, "end": v(22.04, 8.84) * mm});
            skLineSegment(sketch, "E559", {"start": v(22.04, 8.84) * mm, "end": v(22.1, 8.8) * mm});
            skLineSegment(sketch, "E560", {"start": v(22.1, 8.8) * mm, "end": v(22.16, 8.75) * mm});
            skLineSegment(sketch, "E561", {"start": v(22.16, 8.75) * mm, "end": v(22.22, 8.7) * mm});
            skLineSegment(sketch, "E562", {"start": v(22.22, 8.7) * mm, "end": v(22.27, 8.65) * mm});
            skLineSegment(sketch, "E563", {"start": v(22.27, 8.65) * mm, "end": v(22.32, 8.6) * mm});
            skLineSegment(sketch, "E564", {"start": v(22.32, 8.6) * mm, "end": v(22.37, 8.55) * mm});
            skLineSegment(sketch, "E565", {"start": v(22.37, 8.55) * mm, "end": v(22.41, 8.49) * mm});
            skLineSegment(sketch, "E566", {"start": v(22.41, 8.49) * mm, "end": v(22.45, 8.43) * mm});
            skLineSegment(sketch, "E567", {"start": v(22.45, 8.43) * mm, "end": v(22.5, 8.37) * mm});
            skLineSegment(sketch, "E568", {"start": v(22.5, 8.37) * mm, "end": v(22.53, 8.3) * mm});
            skLineSegment(sketch, "E569", {"start": v(22.53, 8.3) * mm, "end": v(22.56, 8.24) * mm});
            skLineSegment(sketch, "E570", {"start": v(22.56, 8.24) * mm, "end": v(22.59, 8.17) * mm});
            skLineSegment(sketch, "E571", {"start": v(22.59, 8.17) * mm, "end": v(22.62, 8.1) * mm});
            skLineSegment(sketch, "E572", {"start": v(22.62, 8.1) * mm, "end": v(22.64, 8.03) * mm});
            skLineSegment(sketch, "E573", {"start": v(22.64, 8.03) * mm, "end": v(22.66, 7.96) * mm});
            skLineSegment(sketch, "E574", {"start": v(22.66, 7.96) * mm, "end": v(22.68, 7.88) * mm});
            skLineSegment(sketch, "E575", {"start": v(22.68, 7.88) * mm, "end": v(22.7, 7.81) * mm});
            skLineSegment(sketch, "E576", {"start": v(22.7, 7.81) * mm, "end": v(22.7, 7.74) * mm});
            skLineSegment(sketch, "E577", {"start": v(22.7, 7.74) * mm, "end": v(22.71, 7.66) * mm});
            skLineSegment(sketch, "E578", {"start": v(22.71, 7.66) * mm, "end": v(22.71, 7.59) * mm});
            skLineSegment(sketch, "E579", {"start": v(34.86, 3.34) * mm, "end": v(34.86, 3.36) * mm});
            skLineSegment(sketch, "E580", {"start": v(34.86, 3.36) * mm, "end": v(34.87, 3.39) * mm});
            skLineSegment(sketch, "E581", {"start": v(34.87, 3.39) * mm, "end": v(34.87, 3.4) * mm});
            skLineSegment(sketch, "E582", {"start": v(34.87, 3.4) * mm, "end": v(34.87, 3.43) * mm});
            skLineSegment(sketch, "E583", {"start": v(34.87, 3.43) * mm, "end": v(34.88, 3.49) * mm});
            skLineSegment(sketch, "E584", {"start": v(34.88, 3.49) * mm, "end": v(34.88, 3.54) * mm});
            skLineSegment(sketch, "E585", {"start": v(34.88, 3.54) * mm, "end": v(34.9, 3.6) * mm});
            skLineSegment(sketch, "E586", {"start": v(34.9, 3.6) * mm, "end": v(34.9, 3.67) * mm});
            skLineSegment(sketch, "E587", {"start": v(34.9, 3.67) * mm, "end": v(34.9, 3.74) * mm});
            skLineSegment(sketch, "E588", {"start": v(34.9, 3.74) * mm, "end": v(34.92, 3.81) * mm});
            skLineSegment(sketch, "E589", {"start": v(34.92, 3.81) * mm, "end": v(34.94, 3.97) * mm});
            skLineSegment(sketch, "E590", {"start": v(34.94, 3.97) * mm, "end": v(34.99, 4.3) * mm});
            skLineSegment(sketch, "E591", {"start": v(34.99, 4.3) * mm, "end": v(35.02, 4.47) * mm});
            skLineSegment(sketch, "E592", {"start": v(35.02, 4.47) * mm, "end": v(35.04, 4.64) * mm});
            skLineSegment(sketch, "E593", {"start": v(35.04, 4.64) * mm, "end": v(35.1, 4.97) * mm});
            skLineSegment(sketch, "E594", {"start": v(35.1, 4.97) * mm, "end": v(35.11, 5.13) * mm});
            skLineSegment(sketch, "E595", {"start": v(35.11, 5.13) * mm, "end": v(35.13, 5.2) * mm});
            skLineSegment(sketch, "E596", {"start": v(35.13, 5.2) * mm, "end": v(35.14, 5.28) * mm});
            skLineSegment(sketch, "E597", {"start": v(35.14, 5.28) * mm, "end": v(35.15, 5.36) * mm});
            skLineSegment(sketch, "E598", {"start": v(35.15, 5.36) * mm, "end": v(35.16, 5.42) * mm});
            skLineSegment(sketch, "E599", {"start": v(35.16, 5.42) * mm, "end": v(35.18, 5.49) * mm});
            skLineSegment(sketch, "E600", {"start": v(35.18, 5.49) * mm, "end": v(35.19, 5.55) * mm});
            skLineSegment(sketch, "E601", {"start": v(35.19, 5.55) * mm, "end": v(35.2, 5.6) * mm});
            skLineSegment(sketch, "E602", {"start": v(35.2, 5.6) * mm, "end": v(35.2, 5.66) * mm});
            skLineSegment(sketch, "E603", {"start": v(35.2, 5.66) * mm, "end": v(35.8, 9.04) * mm});
            skLineSegment(sketch, "E604", {"start": v(35.8, 9.04) * mm, "end": v(33.67, 9.38) * mm});
            skLineSegment(sketch, "E605", {"start": v(33.67, 9.38) * mm, "end": v(33.78, 10) * mm});
            skLineSegment(sketch, "E606", {"start": v(33.78, 10) * mm, "end": v(38.27, 10) * mm});
            skLineSegment(sketch, "E607", {"start": v(38.27, 10) * mm, "end": v(34.95, -8.74) * mm});
            skLineSegment(sketch, "E608", {"start": v(34.95, -8.74) * mm, "end": v(36.51, -9.08) * mm});
            skLineSegment(sketch, "E609", {"start": v(36.51, -9.08) * mm, "end": v(36.4, -9.7) * mm});
            skLineSegment(sketch, "E610", {"start": v(36.4, -9.7) * mm, "end": v(32.45, -9.7) * mm});
            skLineSegment(sketch, "E611", {"start": v(32.45, -9.7) * mm, "end": v(32.85, -7.55) * mm});
            skLineSegment(sketch, "E612", {"start": v(32.85, -7.55) * mm, "end": v(32.56, -7.84) * mm});
            skLineSegment(sketch, "E613", {"start": v(32.56, -7.84) * mm, "end": v(32.28, -8.12) * mm});
            skLineSegment(sketch, "E614", {"start": v(32.28, -8.12) * mm, "end": v(32, -8.38) * mm});
            skLineSegment(sketch, "E615", {"start": v(32, -8.38) * mm, "end": v(31.71, -8.62) * mm});
            skLineSegment(sketch, "E616", {"start": v(31.71, -8.62) * mm, "end": v(31.43, -8.84) * mm});
            skLineSegment(sketch, "E617", {"start": v(31.43, -8.84) * mm, "end": v(31.16, -9.04) * mm});
            skLineSegment(sketch, "E618", {"start": v(31.16, -9.04) * mm, "end": v(30.89, -9.22) * mm});
            skLineSegment(sketch, "E619", {"start": v(30.89, -9.22) * mm, "end": v(30.62, -9.39) * mm});
            skLineSegment(sketch, "E620", {"start": v(30.62, -9.39) * mm, "end": v(30.35, -9.53) * mm});
            skLineSegment(sketch, "E621", {"start": v(30.35, -9.53) * mm, "end": v(30.1, -9.66) * mm});
            skLineSegment(sketch, "E622", {"start": v(30.1, -9.66) * mm, "end": v(29.83, -9.76) * mm});
            skLineSegment(sketch, "E623", {"start": v(29.83, -9.76) * mm, "end": v(29.57, -9.85) * mm});
            skLineSegment(sketch, "E624", {"start": v(29.57, -9.85) * mm, "end": v(29.32, -9.91) * mm});
            skLineSegment(sketch, "E625", {"start": v(29.32, -9.91) * mm, "end": v(29.06, -9.96) * mm});
            skLineSegment(sketch, "E626", {"start": v(29.06, -9.96) * mm, "end": v(28.81, -10) * mm});
            skLineSegment(sketch, "E627", {"start": v(28.81, -10) * mm, "end": v(28.57, -10) * mm});
            skLineSegment(sketch, "E628", {"start": v(28.57, -10) * mm, "end": v(28.36, -10) * mm});
            skLineSegment(sketch, "E629", {"start": v(28.36, -10) * mm, "end": v(28.16, -9.98) * mm});
            skLineSegment(sketch, "E630", {"start": v(28.16, -9.98) * mm, "end": v(27.96, -9.96) * mm});
            skLineSegment(sketch, "E631", {"start": v(27.96, -9.96) * mm, "end": v(27.77, -9.92) * mm});
            skLineSegment(sketch, "E632", {"start": v(27.77, -9.92) * mm, "end": v(27.59, -9.88) * mm});
            skLineSegment(sketch, "E633", {"start": v(27.59, -9.88) * mm, "end": v(27.4, -9.82) * mm});
            skLineSegment(sketch, "E634", {"start": v(27.4, -9.82) * mm, "end": v(27.23, -9.76) * mm});
            skLineSegment(sketch, "E635", {"start": v(27.23, -9.76) * mm, "end": v(27.05, -9.68) * mm});
            skLineSegment(sketch, "E636", {"start": v(27.05, -9.68) * mm, "end": v(26.89, -9.6) * mm});
            skLineSegment(sketch, "E637", {"start": v(26.89, -9.6) * mm, "end": v(26.73, -9.5) * mm});
            skLineSegment(sketch, "E638", {"start": v(26.73, -9.5) * mm, "end": v(26.57, -9.4) * mm});
            skLineSegment(sketch, "E639", {"start": v(26.57, -9.4) * mm, "end": v(26.42, -9.3) * mm});
            skLineSegment(sketch, "E640", {"start": v(26.42, -9.3) * mm, "end": v(26.28, -9.17) * mm});
            skLineSegment(sketch, "E641", {"start": v(26.28, -9.17) * mm, "end": v(26.14, -9.05) * mm});
            skLineSegment(sketch, "E642", {"start": v(26.14, -9.05) * mm, "end": v(26.01, -8.91) * mm});
            skLineSegment(sketch, "E643", {"start": v(26.01, -8.91) * mm, "end": v(25.89, -8.77) * mm});
            skLineSegment(sketch, "E644", {"start": v(25.89, -8.77) * mm, "end": v(25.77, -8.6) * mm});
            skLineSegment(sketch, "E645", {"start": v(25.77, -8.6) * mm, "end": v(25.66, -8.44) * mm});
            skLineSegment(sketch, "E646", {"start": v(25.66, -8.44) * mm, "end": v(25.55, -8.27) * mm});
            skLineSegment(sketch, "E647", {"start": v(25.55, -8.27) * mm, "end": v(25.46, -8.09) * mm});
            skLineSegment(sketch, "E648", {"start": v(25.46, -8.09) * mm, "end": v(25.36, -7.9) * mm});
            skLineSegment(sketch, "E649", {"start": v(25.36, -7.9) * mm, "end": v(25.28, -7.7) * mm});
            skLineSegment(sketch, "E650", {"start": v(25.28, -7.7) * mm, "end": v(25.2, -7.5) * mm});
            skLineSegment(sketch, "E651", {"start": v(25.2, -7.5) * mm, "end": v(25.13, -7.28) * mm});
            skLineSegment(sketch, "E652", {"start": v(25.13, -7.28) * mm, "end": v(25.06, -7.06) * mm});
            skLineSegment(sketch, "E653", {"start": v(25.06, -7.06) * mm, "end": v(25.01, -6.83) * mm});
            skLineSegment(sketch, "E654", {"start": v(25.01, -6.83) * mm, "end": v(24.97, -6.6) * mm});
            skLineSegment(sketch, "E655", {"start": v(24.97, -6.6) * mm, "end": v(24.9, -6.1) * mm});
            skLineSegment(sketch, "E656", {"start": v(24.9, -6.1) * mm, "end": v(24.87, -5.58) * mm});
            skLineSegment(sketch, "E657", {"start": v(24.87, -5.58) * mm, "end": v(24.86, -5.31) * mm});
            skLineSegment(sketch, "E658", {"start": v(24.86, -5.31) * mm, "end": v(24.88, -4.72) * mm});
            skLineSegment(sketch, "E659", {"start": v(24.88, -4.72) * mm, "end": v(24.93, -4.14) * mm});
            skLineSegment(sketch, "E660", {"start": v(24.93, -4.14) * mm, "end": v(25.01, -3.56) * mm});
            skLineSegment(sketch, "E661", {"start": v(25.01, -3.56) * mm, "end": v(25.13, -3) * mm});
            skLineSegment(sketch, "E662", {"start": v(25.13, -3) * mm, "end": v(25.27, -2.44) * mm});
            skLineSegment(sketch, "E663", {"start": v(25.27, -2.44) * mm, "end": v(25.45, -1.9) * mm});
            skLineSegment(sketch, "E664", {"start": v(25.45, -1.9) * mm, "end": v(25.65, -1.37) * mm});
            skLineSegment(sketch, "E665", {"start": v(25.65, -1.37) * mm, "end": v(25.88, -0.86) * mm});
            skLineSegment(sketch, "E666", {"start": v(25.88, -0.86) * mm, "end": v(26.13, -0.37) * mm});
            skLineSegment(sketch, "E667", {"start": v(26.13, -0.37) * mm, "end": v(26.4, 0.1) * mm});
            skLineSegment(sketch, "E668", {"start": v(26.4, 0.1) * mm, "end": v(26.71, 0.54) * mm});
            skLineSegment(sketch, "E669", {"start": v(26.71, 0.54) * mm, "end": v(27.04, 0.96) * mm});
            skLineSegment(sketch, "E670", {"start": v(27.04, 0.96) * mm, "end": v(27.4, 1.36) * mm});
            skLineSegment(sketch, "E671", {"start": v(27.4, 1.36) * mm, "end": v(27.78, 1.73) * mm});
            skLineSegment(sketch, "E672", {"start": v(27.78, 1.73) * mm, "end": v(28.17, 2.07) * mm});
            skLineSegment(sketch, "E673", {"start": v(28.17, 2.07) * mm, "end": v(28.6, 2.39) * mm});
            skLineSegment(sketch, "E674", {"start": v(28.6, 2.39) * mm, "end": v(29.03, 2.67) * mm});
            skLineSegment(sketch, "E675", {"start": v(29.03, 2.67) * mm, "end": v(29.49, 2.93) * mm});
            skLineSegment(sketch, "E676", {"start": v(29.49, 2.93) * mm, "end": v(29.96, 3.14) * mm});
            skLineSegment(sketch, "E677", {"start": v(29.96, 3.14) * mm, "end": v(30.45, 3.33) * mm});
            skLineSegment(sketch, "E678", {"start": v(30.45, 3.33) * mm, "end": v(30.96, 3.47) * mm});
            skLineSegment(sketch, "E679", {"start": v(30.96, 3.47) * mm, "end": v(31.49, 3.58) * mm});
            skLineSegment(sketch, "E680", {"start": v(31.49, 3.58) * mm, "end": v(32.03, 3.64) * mm});
            skLineSegment(sketch, "E681", {"start": v(32.03, 3.64) * mm, "end": v(32.57, 3.66) * mm});
            skLineSegment(sketch, "E682", {"start": v(32.57, 3.66) * mm, "end": v(32.91, 3.66) * mm});
            skLineSegment(sketch, "E683", {"start": v(32.91, 3.66) * mm, "end": v(33.23, 3.64) * mm});
            skLineSegment(sketch, "E684", {"start": v(33.23, 3.64) * mm, "end": v(33.54, 3.61) * mm});
            skLineSegment(sketch, "E685", {"start": v(33.54, 3.61) * mm, "end": v(33.82, 3.58) * mm});
            skLineSegment(sketch, "E686", {"start": v(33.82, 3.58) * mm, "end": v(34.1, 3.53) * mm});
            skLineSegment(sketch, "E687", {"start": v(34.1, 3.53) * mm, "end": v(34.37, 3.48) * mm});
            skLineSegment(sketch, "E688", {"start": v(34.37, 3.48) * mm, "end": v(34.62, 3.41) * mm});
            skLineSegment(sketch, "E689", {"start": v(34.62, 3.41) * mm, "end": v(34.86, 3.34) * mm});
            skLineSegment(sketch, "E690", {"start": v(34.54, 1.9) * mm, "end": v(34.3, 2.05) * mm});
            skLineSegment(sketch, "E691", {"start": v(34.3, 2.05) * mm, "end": v(34.05, 2.18) * mm});
            skLineSegment(sketch, "E692", {"start": v(34.05, 2.18) * mm, "end": v(33.8, 2.3) * mm});
            skLineSegment(sketch, "E693", {"start": v(33.8, 2.3) * mm, "end": v(33.55, 2.4) * mm});
            skLineSegment(sketch, "E694", {"start": v(33.55, 2.4) * mm, "end": v(33.41, 2.44) * mm});
            skLineSegment(sketch, "E695", {"start": v(33.41, 2.44) * mm, "end": v(33.27, 2.48) * mm});
            skLineSegment(sketch, "E696", {"start": v(33.27, 2.48) * mm, "end": v(33.13, 2.5) * mm});
            skLineSegment(sketch, "E697", {"start": v(33.13, 2.5) * mm, "end": v(32.98, 2.53) * mm});
            skLineSegment(sketch, "E698", {"start": v(32.98, 2.53) * mm, "end": v(32.82, 2.55) * mm});
            skLineSegment(sketch, "E699", {"start": v(32.82, 2.55) * mm, "end": v(32.65, 2.57) * mm});
            skLineSegment(sketch, "E700", {"start": v(32.65, 2.57) * mm, "end": v(32.48, 2.58) * mm});
            skLineSegment(sketch, "E701", {"start": v(32.48, 2.58) * mm, "end": v(32.3, 2.58) * mm});
            skLineSegment(sketch, "E702", {"start": v(32.3, 2.58) * mm, "end": v(32.11, 2.57) * mm});
            skLineSegment(sketch, "E703", {"start": v(32.11, 2.57) * mm, "end": v(31.93, 2.56) * mm});
            skLineSegment(sketch, "E704", {"start": v(31.93, 2.56) * mm, "end": v(31.75, 2.53) * mm});
            skLineSegment(sketch, "E705", {"start": v(31.75, 2.53) * mm, "end": v(31.57, 2.5) * mm});
            skLineSegment(sketch, "E706", {"start": v(31.57, 2.5) * mm, "end": v(31.4, 2.46) * mm});
            skLineSegment(sketch, "E707", {"start": v(31.4, 2.46) * mm, "end": v(31.23, 2.4) * mm});
            skLineSegment(sketch, "E708", {"start": v(31.23, 2.4) * mm, "end": v(31.06, 2.34) * mm});
            skLineSegment(sketch, "E709", {"start": v(31.06, 2.34) * mm, "end": v(30.9, 2.26) * mm});
            skLineSegment(sketch, "E710", {"start": v(30.9, 2.26) * mm, "end": v(30.73, 2.18) * mm});
            skLineSegment(sketch, "E711", {"start": v(30.73, 2.18) * mm, "end": v(30.42, 1.99) * mm});
            skLineSegment(sketch, "E712", {"start": v(30.42, 1.99) * mm, "end": v(30.12, 1.77) * mm});
            skLineSegment(sketch, "E713", {"start": v(30.12, 1.77) * mm, "end": v(29.83, 1.52) * mm});
            skLineSegment(sketch, "E714", {"start": v(29.83, 1.52) * mm, "end": v(29.69, 1.39) * mm});
            skLineSegment(sketch, "E715", {"start": v(29.69, 1.39) * mm, "end": v(29.42, 1.1) * mm});
            skLineSegment(sketch, "E716", {"start": v(29.42, 1.1) * mm, "end": v(29.16, 0.8) * mm});
            skLineSegment(sketch, "E717", {"start": v(29.16, 0.8) * mm, "end": v(28.92, 0.47) * mm});
            skLineSegment(sketch, "E718", {"start": v(28.92, 0.47) * mm, "end": v(28.7, 0.11) * mm});
            skLineSegment(sketch, "E719", {"start": v(28.7, 0.11) * mm, "end": v(28.48, -0.26) * mm});
            skLineSegment(sketch, "E720", {"start": v(28.48, -0.26) * mm, "end": v(28.3, -0.65) * mm});
            skLineSegment(sketch, "E721", {"start": v(28.3, -0.65) * mm, "end": v(28.12, -1.05) * mm});
            skLineSegment(sketch, "E722", {"start": v(28.12, -1.05) * mm, "end": v(27.96, -1.47) * mm});
            skLineSegment(sketch, "E723", {"start": v(27.96, -1.47) * mm, "end": v(27.81, -1.9) * mm});
            skLineSegment(sketch, "E724", {"start": v(27.81, -1.9) * mm, "end": v(27.58, -2.77) * mm});
            skLineSegment(sketch, "E725", {"start": v(27.58, -2.77) * mm, "end": v(27.48, -3.22) * mm});
            skLineSegment(sketch, "E726", {"start": v(27.48, -3.22) * mm, "end": v(27.42, -3.67) * mm});
            skLineSegment(sketch, "E727", {"start": v(27.42, -3.67) * mm, "end": v(27.34, -4.56) * mm});
            skLineSegment(sketch, "E728", {"start": v(27.34, -4.56) * mm, "end": v(27.33, -5) * mm});
            skLineSegment(sketch, "E729", {"start": v(27.33, -5) * mm, "end": v(27.33, -5.22) * mm});
            skLineSegment(sketch, "E730", {"start": v(27.33, -5.22) * mm, "end": v(27.34, -5.43) * mm});
            skLineSegment(sketch, "E731", {"start": v(27.34, -5.43) * mm, "end": v(27.36, -5.63) * mm});
            skLineSegment(sketch, "E732", {"start": v(27.36, -5.63) * mm, "end": v(27.38, -5.82) * mm});
            skLineSegment(sketch, "E733", {"start": v(27.38, -5.82) * mm, "end": v(27.4, -6) * mm});
            skLineSegment(sketch, "E734", {"start": v(27.4, -6) * mm, "end": v(27.44, -6.18) * mm});
            skLineSegment(sketch, "E735", {"start": v(27.44, -6.18) * mm, "end": v(27.48, -6.34) * mm});
            skLineSegment(sketch, "E736", {"start": v(27.48, -6.34) * mm, "end": v(27.53, -6.5) * mm});
            skLineSegment(sketch, "E737", {"start": v(27.53, -6.5) * mm, "end": v(27.58, -6.65) * mm});
            skLineSegment(sketch, "E738", {"start": v(27.58, -6.65) * mm, "end": v(27.63, -6.8) * mm});
            skLineSegment(sketch, "E739", {"start": v(27.63, -6.8) * mm, "end": v(27.69, -6.93) * mm});
            skLineSegment(sketch, "E740", {"start": v(27.69, -6.93) * mm, "end": v(27.75, -7.06) * mm});
            skLineSegment(sketch, "E741", {"start": v(27.75, -7.06) * mm, "end": v(27.81, -7.19) * mm});
            skLineSegment(sketch, "E742", {"start": v(27.81, -7.19) * mm, "end": v(27.88, -7.3) * mm});
            skLineSegment(sketch, "E743", {"start": v(27.88, -7.3) * mm, "end": v(27.95, -7.41) * mm});
            skLineSegment(sketch, "E744", {"start": v(27.95, -7.41) * mm, "end": v(28.03, -7.52) * mm});
            skLineSegment(sketch, "E745", {"start": v(28.03, -7.52) * mm, "end": v(28.1, -7.61) * mm});
            skLineSegment(sketch, "E746", {"start": v(28.1, -7.61) * mm, "end": v(28.2, -7.7) * mm});
            skLineSegment(sketch, "E747", {"start": v(28.2, -7.7) * mm, "end": v(28.28, -7.78) * mm});
            skLineSegment(sketch, "E748", {"start": v(28.28, -7.78) * mm, "end": v(28.37, -7.85) * mm});
            skLineSegment(sketch, "E749", {"start": v(28.37, -7.85) * mm, "end": v(28.46, -7.92) * mm});
            skLineSegment(sketch, "E750", {"start": v(28.46, -7.92) * mm, "end": v(28.55, -7.98) * mm});
            skLineSegment(sketch, "E751", {"start": v(28.55, -7.98) * mm, "end": v(28.65, -8.04) * mm});
            skLineSegment(sketch, "E752", {"start": v(28.65, -8.04) * mm, "end": v(28.75, -8.09) * mm});
            skLineSegment(sketch, "E753", {"start": v(28.75, -8.09) * mm, "end": v(28.85, -8.13) * mm});
            skLineSegment(sketch, "E754", {"start": v(28.85, -8.13) * mm, "end": v(28.96, -8.16) * mm});
            skLineSegment(sketch, "E755", {"start": v(28.96, -8.16) * mm, "end": v(29.06, -8.2) * mm});
            skLineSegment(sketch, "E756", {"start": v(29.06, -8.2) * mm, "end": v(29.17, -8.22) * mm});
            skLineSegment(sketch, "E757", {"start": v(29.17, -8.22) * mm, "end": v(29.27, -8.24) * mm});
            skLineSegment(sketch, "E758", {"start": v(29.27, -8.24) * mm, "end": v(29.38, -8.26) * mm});
            skLineSegment(sketch, "E759", {"start": v(29.38, -8.26) * mm, "end": v(29.49, -8.26) * mm});
            skLineSegment(sketch, "E760", {"start": v(29.49, -8.26) * mm, "end": v(29.6, -8.27) * mm});
            skLineSegment(sketch, "E761", {"start": v(29.6, -8.27) * mm, "end": v(29.79, -8.26) * mm});
            skLineSegment(sketch, "E762", {"start": v(29.79, -8.26) * mm, "end": v(29.99, -8.24) * mm});
            skLineSegment(sketch, "E763", {"start": v(29.99, -8.24) * mm, "end": v(30.2, -8.2) * mm});
            skLineSegment(sketch, "E764", {"start": v(30.2, -8.2) * mm, "end": v(30.4, -8.14) * mm});
            skLineSegment(sketch, "E765", {"start": v(30.4, -8.14) * mm, "end": v(30.61, -8.07) * mm});
            skLineSegment(sketch, "E766", {"start": v(30.61, -8.07) * mm, "end": v(30.83, -7.99) * mm});
            skLineSegment(sketch, "E767", {"start": v(30.83, -7.99) * mm, "end": v(31.05, -7.88) * mm});
            skLineSegment(sketch, "E768", {"start": v(31.05, -7.88) * mm, "end": v(31.27, -7.77) * mm});
            skLineSegment(sketch, "E769", {"start": v(31.27, -7.77) * mm, "end": v(31.5, -7.63) * mm});
            skLineSegment(sketch, "E770", {"start": v(31.5, -7.63) * mm, "end": v(31.72, -7.49) * mm});
            skLineSegment(sketch, "E771", {"start": v(31.72, -7.49) * mm, "end": v(31.95, -7.33) * mm});
            skLineSegment(sketch, "E772", {"start": v(31.95, -7.33) * mm, "end": v(32.17, -7.15) * mm});
            skLineSegment(sketch, "E773", {"start": v(32.17, -7.15) * mm, "end": v(32.39, -6.97) * mm});
            skLineSegment(sketch, "E774", {"start": v(32.39, -6.97) * mm, "end": v(32.82, -6.56) * mm});
            skLineSegment(sketch, "E775", {"start": v(32.82, -6.56) * mm, "end": v(33.03, -6.34) * mm});
            skLineSegment(sketch, "E776", {"start": v(33.03, -6.34) * mm, "end": v(34.54, 1.9) * mm});
            skSolve(sketch);
        }
        {
            var Q0;
            Q0=makeQuery(id+"F0.imprint","IMPRINT",FACE,{"disambiguationData":[TD([[makeQuery(id+"F0.imprint","IMPRINT",EDGE,{"derivedFrom":sQuery(id+"F0.wireOp",EDGE,"9c274906-66f2-47cc-ba81-bc829715841a")}),-1.0]])]});
            var Q1;
            {var subQ1=sQuery(id+"F0.wireOp",EDGE,"E3");Q1=makeQuery(id+"F0.imprint","IMPRINT",FACE,{"disambiguationData":[TD([[makeQuery(id+"F0.imprint","IMPRINT",EDGE,{"derivedFrom":subQ1}),-1.0]])]});}
            var Q2;
            Q2=makeQuery(id+"F0.imprint","IMPRINT",FACE,{"disambiguationData":[TD([[makeQuery(id+"F0.imprint","IMPRINT",EDGE,{"derivedFrom":sQuery(id+"F0.wireOp",EDGE,"6ab65d4b-20cc-4260-84e2-1f812e6f8199")}),1.0]])]});
            var Q3;
            Q3=makeQuery(id+"F0.imprint","IMPRINT",FACE,{"disambiguationData":[TD([[makeQuery(id+"F0.imprint","IMPRINT",EDGE,{"derivedFrom":sQuery(id+"F0.wireOp",EDGE,"fbc92326-29e4-4a65-8bcc-6a279c66f74b")}),-1.0]])]});
            var Q4;
            Q4=makeQuery(id+"F0.imprint","IMPRINT",FACE,{"disambiguationData":[TD([[makeQuery(id+"F0.imprint","IMPRINT",EDGE,{"derivedFrom":sQuery(id+"F0.wireOp",EDGE,"E1")}),1.0]])]});
            var Q5;
            Q5=makeQuery(id+"F0.imprint","IMPRINT",FACE,{"disambiguationData":[TD([[makeQuery(id+"F0.imprint","IMPRINT",EDGE,{"derivedFrom":sQuery(id+"F0.wireOp",EDGE,"edff43eb-599a-4c31-8809-e4d85603c349")}),-1.0]])]});
            var Q6;
            Q6=makeQuery(id+"F0.imprint","IMPRINT",FACE,{"disambiguationData":[TD([[makeQuery(id+"F0.imprint","IMPRINT",EDGE,{"derivedFrom":sQuery(id+"F0.wireOp",EDGE,"9c1aa12f-a708-4583-be26-2b383a722471")}),1.0]])]});
            var Q7;
            Q7=makeQuery(id+"F0.imprint","IMPRINT",FACE,{"disambiguationData":[TD([[makeQuery(id+"F0.imprint","IMPRINT",EDGE,{"derivedFrom":sQuery(id+"F0.wireOp",EDGE,"d64aa239-00f7-4386-9746-6503c5a989f5")}),-1.0]])]});
            var Q8;
            {var subQ5=sQuery(id+"F0.wireOp",EDGE,"a99f0830-5d0a-4233-9662-b7695eaebfe7");Q8=makeQuery(id+"F0.imprint","IMPRINT",FACE,{"disambiguationData":[TD([[makeQuery(id+"F0.imprint","IMPRINT",EDGE,{"derivedFrom":subQ5}),-1.0]])]});}
            var Q9;
            Q9=makeQuery(id+"F0.imprint","IMPRINT",FACE,{"disambiguationData":[TD([[makeQuery(id+"F0.imprint","IMPRINT",EDGE,{"derivedFrom":sQuery(id+"F0.wireOp",EDGE,"2a4fbe35-dfba-4a85-95bd-e9da396d757a")}),-1.0]])]});
            var Q10;
            Q10=makeQuery(id+"F0.imprint","IMPRINT",FACE,{"disambiguationData":[TD([[makeQuery(id+"F0.imprint","IMPRINT",EDGE,{"derivedFrom":sQuery(id+"F0.wireOp",EDGE,"2a4fbe35-dfba-4a85-95bd-e9da396d757a")}),1.0]])]});
            var Q11;
            Q11=makeQuery(id+"F0.imprint","IMPRINT",FACE,{"disambiguationData":[TD([[makeQuery(id+"F0.imprint","IMPRINT",EDGE,{"derivedFrom":sQuery(id+"F0.wireOp",EDGE,"7aec7717-0c6f-4bae-bb6d-1404d206293c")}),-1.0]])]});
            var Q12;
            Q12=makeQuery(id+"F0.imprint","IMPRINT",FACE,{"disambiguationData":[TD([[makeQuery(id+"F0.imprint","IMPRINT",EDGE,{"derivedFrom":sQuery(id+"F0.wireOp",EDGE,"2e831668-c073-46cd-8cf9-afdbba8640c2")}),-1.0]])]});
            var Q13;
            Q13=makeQuery(id+"F0.imprint","IMPRINT",FACE,{"disambiguationData":[TD([[makeQuery(id+"F0.imprint","IMPRINT",EDGE,{"derivedFrom":sQuery(id+"F0.wireOp",EDGE,"0ff61a9d-bce7-4498-a74a-3b659cdb3a31")}),1.0]])]});
            var Q14;
            Q14=makeQuery(id+"F0.imprint","IMPRINT",FACE,{"disambiguationData":[TD([[makeQuery(id+"F0.imprint","IMPRINT",EDGE,{"derivedFrom":sQuery(id+"F0.wireOp",EDGE,"E5")}),-1.0]])]});
            var Q15;
            Q15=makeQuery(id+"F0.imprint","IMPRINT",FACE,{"disambiguationData":[TD([[makeQuery(id+"F0.imprint","IMPRINT",EDGE,{"derivedFrom":sQuery(id+"F0.wireOp",EDGE,"E24")}),-1.0]])]});
            var Q16;
            Q16=makeQuery(id+"F0.imprint","IMPRINT",FACE,{"disambiguationData":[TD([[makeQuery(id+"F0.imprint","IMPRINT",EDGE,{"derivedFrom":sQuery(id+"F0.wireOp",EDGE,"E278")}),-1.0]])]});
            var Q17;
            Q17=makeQuery(id+"F0.imprint","IMPRINT",FACE,{"disambiguationData":[TD([[makeQuery(id+"F0.imprint","IMPRINT",EDGE,{"derivedFrom":sQuery(id+"F0.wireOp",EDGE,"E387")}),-1.0]])]});
            var Q18;
            Q18=makeQuery(id+"F0.imprint","IMPRINT",FACE,{"disambiguationData":[TD([[makeQuery(id+"F0.imprint","IMPRINT",EDGE,{"derivedFrom":sQuery(id+"F0.wireOp",EDGE,"E451")}),-1.0]])]});
            var Q19;
            Q19=makeQuery(id+"F0.imprint","IMPRINT",FACE,{"disambiguationData":[TD([[makeQuery(id+"F0.imprint","IMPRINT",EDGE,{"derivedFrom":sQuery(id+"F0.wireOp",EDGE,"E579")}),-1.0]])]});
            var Q20;
            Q20=makeQuery(id+"F0.imprint","IMPRINT",FACE,{"disambiguationData":[TD([[makeQuery(id+"F0.imprint","IMPRINT",EDGE,{"derivedFrom":sQuery(id+"F0.wireOp",EDGE,"E21")}),1.0]])]});
            var Q21;
            Q21=makeQuery(id+"F0.imprint","IMPRINT",FACE,{"disambiguationData":[TD([[makeQuery(id+"F0.imprint","IMPRINT",EDGE,{"derivedFrom":sQuery(id+"F0.wireOp",EDGE,"E690")}),1.0]])]});
            var Q22;
            Q22=makeQuery(id+"F0.imprint","IMPRINT",FACE,{"disambiguationData":[TD([[makeQuery(id+"F0.imprint","IMPRINT",EDGE,{"derivedFrom":sQuery(id+"F0.wireOp",EDGE,"E459")}),-1.0]])]});
            extrude(context, id + "F1", {"entities" : qUnion([Q0, Q1, Q2, Q3, Q4, Q5, Q6, Q7, Q8, Q9, Q10, Q11, Q12, Q13, Q14, Q15, Q16, Q17, Q18, Q19, Q20, Q21, Q22]), "oppositeDirection" : true, "depth" : 1.6 * mm, "offsetDistance" : 25 * mm});
        }
        {
            var Q0;
            Q0=makeQuery(id+"F0.imprint","IMPRINT",FACE,{"disambiguationData":[TD([[makeQuery(id+"F0.imprint","IMPRINT",EDGE,{"derivedFrom":sQuery(id+"F0.wireOp",EDGE,"E1")}),1.0]])]});
            extrude(context, id + "F2", {"entities" : qUnion([Q0]), "operationType" : NewBodyOperationType.ADD, "depth" : 1.6 * mm, "offsetDistance" : 25 * mm});
        }
        {
            var Q0;
            Q0=makeQuery(id+"F0.imprint","IMPRINT",FACE,{"disambiguationData":[TD([[makeQuery(id+"F0.imprint","IMPRINT",EDGE,{"derivedFrom":sQuery(id+"F0.wireOp",EDGE,"E5")}),-1.0]])]});
            var Q1;
            Q1=makeQuery(id+"F0.imprint","IMPRINT",FACE,{"disambiguationData":[TD([[makeQuery(id+"F0.imprint","IMPRINT",EDGE,{"derivedFrom":sQuery(id+"F0.wireOp",EDGE,"E24")}),-1.0]])]});
            var Q2;
            Q2=makeQuery(id+"F0.imprint","IMPRINT",FACE,{"disambiguationData":[TD([[makeQuery(id+"F0.imprint","IMPRINT",EDGE,{"derivedFrom":sQuery(id+"F0.wireOp",EDGE,"E278")}),-1.0]])]});
            var Q3;
            Q3=makeQuery(id+"F0.imprint","IMPRINT",FACE,{"disambiguationData":[TD([[makeQuery(id+"F0.imprint","IMPRINT",EDGE,{"derivedFrom":sQuery(id+"F0.wireOp",EDGE,"E387")}),-1.0]])]});
            var Q4;
            Q4=makeQuery(id+"F0.imprint","IMPRINT",FACE,{"disambiguationData":[TD([[makeQuery(id+"F0.imprint","IMPRINT",EDGE,{"derivedFrom":sQuery(id+"F0.wireOp",EDGE,"E451")}),-1.0]])]});
            var Q5;
            Q5=makeQuery(id+"F0.imprint","IMPRINT",FACE,{"disambiguationData":[TD([[makeQuery(id+"F0.imprint","IMPRINT",EDGE,{"derivedFrom":sQuery(id+"F0.wireOp",EDGE,"E579")}),-1.0]])]});
            extrude(context, id + "F3", {"entities" : qUnion([Q0, Q1, Q2, Q3, Q4, Q5]), "operationType" : NewBodyOperationType.ADD, "depth" : 1 * mm, "offsetDistance" : 25 * mm});
        }
    });
